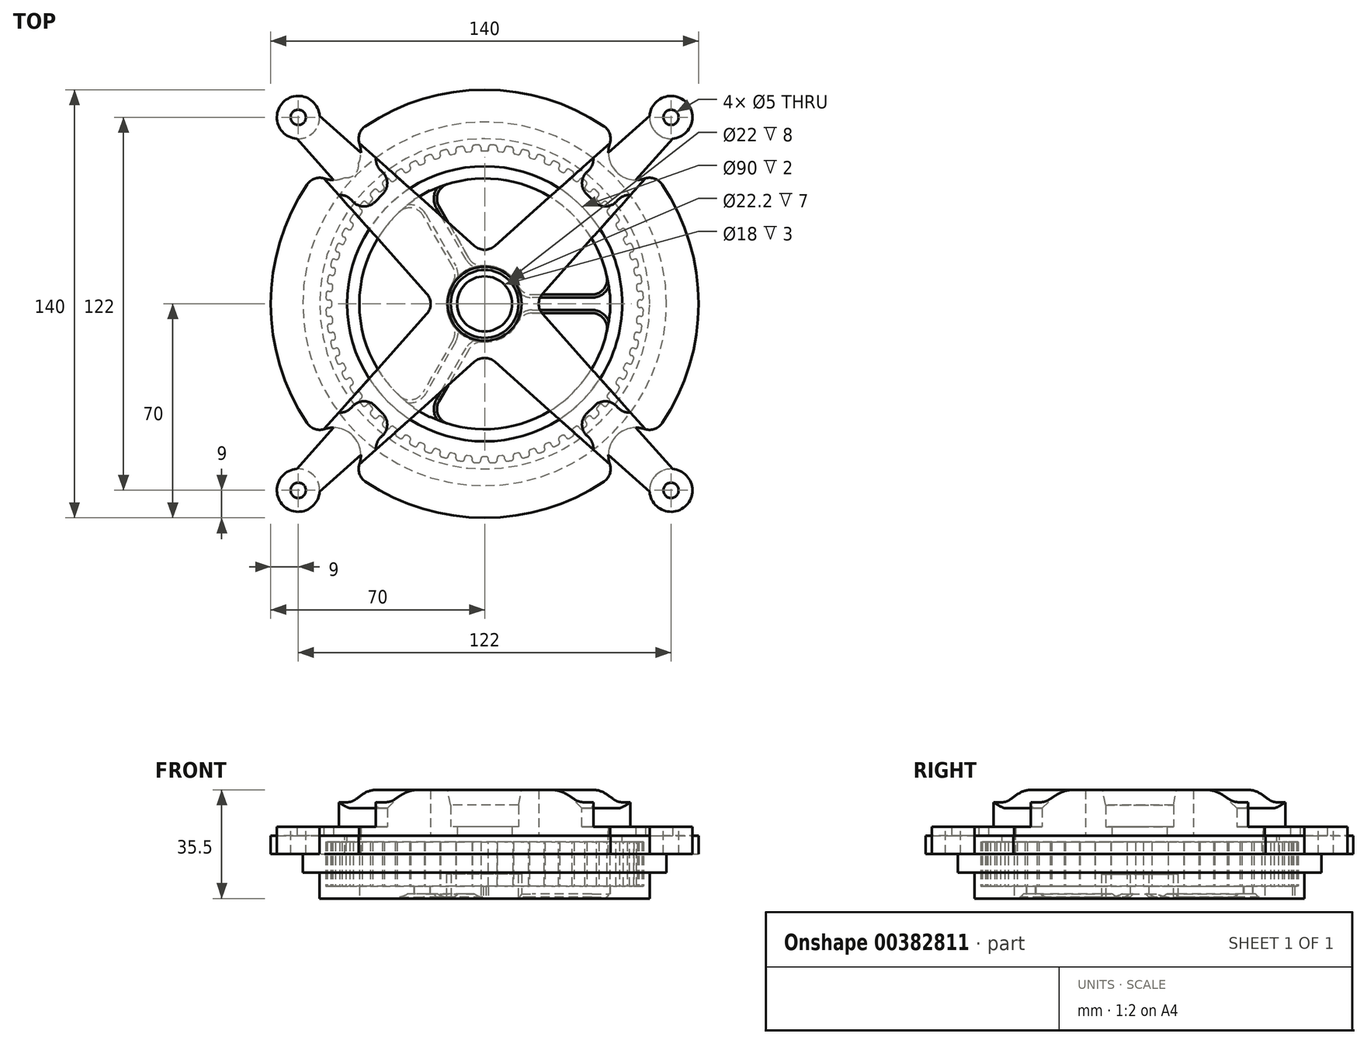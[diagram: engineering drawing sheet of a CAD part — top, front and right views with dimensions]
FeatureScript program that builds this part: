
annotation { "Feature Type Name" : "Feature", "Feature Type Description" : "" }
export const myFeature = defineFeature(function(context is Context, id is Id, definition is map)
    precondition{}
    {
        {
            var Q0;
            Q0=qCreatedBy(makeId("Top.planeOp"),FACE);
            var sketch = newSketch(context, id + "F0", { "sketchPlane" : qUnion([Q0])});
            skCircle(sketch, "E0", {"center": v(0, 0) * mm, "radius": 54 * mm});
            skCircle(sketch, "E1", {"center": v(0, 0) * mm, "radius": 52 * mm});
            skLineSegment(sketch, "E2.bottom", {"start": v(-1.25, 54) * mm, "end": v(1.25, 54) * mm});
            skLineSegment(sketch, "E2.top", {"start": v(-1.25, 50) * mm, "end": v(1.25, 50) * mm});
            skLineSegment(sketch, "E2.left", {"start": v(-1.25, 54) * mm, "end": v(-1.25, 50) * mm});
            skLineSegment(sketch, "E2.right", {"start": v(1.25, 54) * mm, "end": v(1.25, 50) * mm});
            skPoint(sketch, "E2.middle", {"position": v(0, 52) * mm});
            skCircle(sketch, "E3", {"center": v(0, 0) * mm, "radius": 57 * mm});
            skCircle(sketch, "E4", {"center": v(0, 0) * mm, "radius": 41 * mm});
            skCircle(sketch, "E5", {"center": v(0, 0) * mm, "radius": 9 * mm});
            skCircle(sketch, "E6", {"center": v(0, 0) * mm, "radius": 11 * mm});
            skCircle(sketch, "E7", {"center": v(0, 0) * mm, "radius": 12.5 * mm});
            skPoint(sketch, "E8.middle", {"position": v(-23.12, 0) * mm});
            skLineSegment(sketch, "E9.bottom", {"start": v(12.13, 3) * mm, "end": v(41.13, 3) * mm});
            skLineSegment(sketch, "E9.top", {"start": v(12.13, -3) * mm, "end": v(41.13, -3) * mm});
            skLineSegment(sketch, "E9.left", {"start": v(12.13, 3) * mm, "end": v(12.13, -3) * mm});
            skLineSegment(sketch, "E9.right", {"start": v(41.13, 3) * mm, "end": v(41.13, -3) * mm});
            skPoint(sketch, "E9.middle", {"position": v(26.63, 0) * mm});
            skLineSegment(sketch, "E10.1.0", {"start": v(-8.67, 9) * mm, "end": v(-23.17, 34.12) * mm});
            skLineSegment(sketch, "E10.1.1", {"start": v(-3.47, 12) * mm, "end": v(-17.97, 37.12) * mm});
            skLineSegment(sketch, "E10.1.2", {"start": v(-23.17, 34.12) * mm, "end": v(-17.97, 37.12) * mm});
            skLineSegment(sketch, "E10.2.0", {"start": v(-3.47, -12) * mm, "end": v(-17.97, -37.12) * mm});
            skLineSegment(sketch, "E10.2.1", {"start": v(-8.67, -9) * mm, "end": v(-23.17, -34.12) * mm});
            skLineSegment(sketch, "E10.2.2", {"start": v(-17.97, -37.12) * mm, "end": v(-23.17, -34.12) * mm});
            skSolve(sketch);
        }
        {
            var Q0;
            Q0=makeQuery(id+"F0.imprint","IMPRINT",FACE,{"disambiguationData":[TD([[makeQuery(id+"F0.imprint","IMPRINT",EDGE,{"derivedFrom":sQuery(id+"F0.wireOp",EDGE,"E0")}),1.0]])]});
            var Q1;
            {var subQ5=sQuery(id+"F0.wireOp",EDGE,"E2.top");Q1=makeQuery(id+"F0.imprint","IMPRINT",FACE,{"disambiguationData":[TD([[makeQuery(id+"F0.imprint","IMPRINT",EDGE,{"derivedFrom":subQ5}),1.0]])]});}
            var Q2;
            {var subQ0=sQuery(id+"F0.wireOp",EDGE,"E2.right");var subQ1=sQuery(id+"F0.wireOp",EDGE,"E0");var subQ2=makeQuery(id+"F0.imprint","INTERSECT",VERTEX,{"derivedFrom":[subQ1,subQ0]});Q2=makeQuery(id+"F0.imprint","IMPRINT",FACE,{"disambiguationData":[TD([[makeQuery(id+"F0.imprint","IMPRINT",EDGE,{"disambiguationData":[TD([[subQ2,1.0]])],"derivedFrom":subQ1}),1.0]])]});}
            extrude(context, id + "F1", {"entities" : qUnion([Q0, Q1, Q2]), "depth" : 8 * mm});
        }
        {
            var Q0;
            Q0=makeQuery(id+"F1.opExtrude","SWEPT_EDGE",EDGE,{"disambiguationData":[OSD([sQuery(id+"F0.wireOp",EDGE,"E2.top"),sQuery(id+"F0.wireOp",EDGE,"E2.left")])]});
            var Q1;
            Q1=makeQuery(id+"F1.opExtrude","SWEPT_EDGE",EDGE,{"disambiguationData":[OSD([sQuery(id+"F0.wireOp",EDGE,"E2.top"),sQuery(id+"F0.wireOp",EDGE,"E2.right")])]});
            var Q2;
            Q2=makeQuery(id+"F1.opExtrude","SWEPT_EDGE",EDGE,{"disambiguationData":[OSD([sQuery(id+"F0.wireOp",EDGE,"E1"),sQuery(id+"F0.wireOp",EDGE,"E2.left")])]});
            var Q3;
            Q3=makeQuery(id+"F1.opExtrude","SWEPT_EDGE",EDGE,{"disambiguationData":[OSD([sQuery(id+"F0.wireOp",EDGE,"E1"),sQuery(id+"F0.wireOp",EDGE,"E2.right")])]});
            fillet(context, id + "F2", {"entities" : qUnion([Q0, Q1, Q2, Q3]), "radius" : 0.8 * mm, "tangentPropagation" : true, "allowEdgeOverflow" : false});
        }
        {
            var Q0;
            Q0=makeQuery(id+"F1.opExtrude","SWEPT_BODY",BODY,{"disambiguationData":[OSD([sQuery(id+"F0.wireOp",EDGE,"E0"),sQuery(id+"F0.wireOp",EDGE,"E1"),sQuery(id+"F0.wireOp",EDGE,"E2.top"),sQuery(id+"F0.wireOp",EDGE,"E2.left"),sQuery(id+"F0.wireOp",EDGE,"E2.right")])]});
            var Q1;
            Q1=makeQuery(id+"F1.opExtrude","SWEPT_FACE",FACE,{"disambiguationData":[OSD([sQuery(id+"F0.wireOp",EDGE,"E0")])]});
            circularPattern(context, id + "F3", {"operationType" : NewBodyOperationType.ADD, "entities" : qUnion([Q0]), "axis" : qUnion([Q1]), "angle" : 360 * degree, "instanceCount" : 60, "equalSpace" : true});
        }
        {
            var Q0;
            {var subQ0=sQuery(id+"F0.wireOp",EDGE,"E10.1.1");var subQ1=sQuery(id+"F0.wireOp",EDGE,"E4");var subQ2=makeQuery(id+"F0.imprint","INTERSECT",VERTEX,{"derivedFrom":[subQ1,subQ0]});Q0=makeQuery(id+"F0.imprint","IMPRINT",FACE,{"disambiguationData":[TD([[makeQuery(id+"F0.imprint","IMPRINT",EDGE,{"disambiguationData":[TD([[subQ2,-1.0]])],"derivedFrom":subQ1}),1.0]])]});}
            var Q1;
            {var subQ0=sQuery(id+"F0.wireOp",EDGE,"E10.2.1");var subQ1=sQuery(id+"F0.wireOp",EDGE,"E4");var subQ2=makeQuery(id+"F0.imprint","INTERSECT",VERTEX,{"derivedFrom":[subQ1,subQ0]});Q1=makeQuery(id+"F0.imprint","IMPRINT",FACE,{"disambiguationData":[TD([[makeQuery(id+"F0.imprint","IMPRINT",EDGE,{"disambiguationData":[TD([[subQ2,-1.0]])],"derivedFrom":subQ1}),1.0]])]});}
            var Q2;
            {var subQ0=sQuery(id+"F0.wireOp",EDGE,"E9.bottom");var subQ1=sQuery(id+"F0.wireOp",EDGE,"E4");var subQ2=makeQuery(id+"F0.imprint","INTERSECT",VERTEX,{"derivedFrom":[subQ1,subQ0]});Q2=makeQuery(id+"F0.imprint","IMPRINT",FACE,{"disambiguationData":[TD([[makeQuery(id+"F0.imprint","IMPRINT",EDGE,{"disambiguationData":[TD([[subQ2,1.0]])],"derivedFrom":subQ1}),1.0]])]});}
            var Q3;
            {var subQ0=sQuery(id+"F0.wireOp",EDGE,"E10.1.1");var subQ1=sQuery(id+"F0.wireOp",EDGE,"E4");var subQ2=makeQuery(id+"F0.imprint","INTERSECT",VERTEX,{"derivedFrom":[subQ1,subQ0]});Q3=makeQuery(id+"F0.imprint","IMPRINT",FACE,{"disambiguationData":[TD([[makeQuery(id+"F0.imprint","IMPRINT",EDGE,{"disambiguationData":[TD([[subQ2,-1.0]])],"derivedFrom":subQ1}),1.0]])]});}
            var Q4;
            {var subQ0=sQuery(id+"F0.wireOp",EDGE,"E10.2.1");var subQ1=sQuery(id+"F0.wireOp",EDGE,"E4");var subQ2=makeQuery(id+"F0.imprint","INTERSECT",VERTEX,{"derivedFrom":[subQ1,subQ0]});Q4=makeQuery(id+"F0.imprint","IMPRINT",FACE,{"disambiguationData":[TD([[makeQuery(id+"F0.imprint","IMPRINT",EDGE,{"disambiguationData":[TD([[subQ2,-1.0]])],"derivedFrom":subQ1}),1.0]])]});}
            var Q5;
            {var subQ0=sQuery(id+"F0.wireOp",EDGE,"E9.bottom");var subQ1=sQuery(id+"F0.wireOp",EDGE,"E4");var subQ2=makeQuery(id+"F0.imprint","INTERSECT",VERTEX,{"derivedFrom":[subQ1,subQ0]});Q5=makeQuery(id+"F0.imprint","IMPRINT",FACE,{"disambiguationData":[TD([[makeQuery(id+"F0.imprint","IMPRINT",EDGE,{"disambiguationData":[TD([[subQ2,1.0]])],"derivedFrom":subQ1}),1.0]])]});}
            var Q6;
            {var subQ2=sQuery(id+"F0.wireOp",EDGE,"E2.top");Q6=makeQuery(id+"F0.imprint","IMPRINT",FACE,{"disambiguationData":[TD([[makeQuery(id+"F0.imprint","IMPRINT",EDGE,{"derivedFrom":subQ2}),-1.0]])]});}
            var Q7;
            {var subQ2=sQuery(id+"F0.wireOp",EDGE,"E2.top");Q7=makeQuery(id+"F0.imprint","IMPRINT",FACE,{"disambiguationData":[TD([[makeQuery(id+"F0.imprint","IMPRINT",EDGE,{"derivedFrom":subQ2}),-1.0]])]});}
            var Q8;
            {var subQ5=sQuery(id+"F0.wireOp",EDGE,"E10.1.2");Q8=makeQuery(id+"F0.imprint","IMPRINT",FACE,{"disambiguationData":[TD([[makeQuery(id+"F0.imprint","IMPRINT",EDGE,{"derivedFrom":subQ5}),-1.0]])]});}
            var Q9;
            {var subQ0=sQuery(id+"F0.wireOp",EDGE,"E10.1.1");var subQ1=sQuery(id+"F0.wireOp",EDGE,"E4");var subQ2=makeQuery(id+"F0.imprint","INTERSECT",VERTEX,{"derivedFrom":[subQ1,subQ0]});Q9=makeQuery(id+"F0.imprint","IMPRINT",FACE,{"disambiguationData":[TD([[makeQuery(id+"F0.imprint","IMPRINT",EDGE,{"disambiguationData":[TD([[subQ2,-1.0]])],"derivedFrom":subQ1}),1.0]])]});}
            var Q10;
            {var subQ5=sQuery(id+"F0.wireOp",EDGE,"E9.right");Q10=makeQuery(id+"F0.imprint","IMPRINT",FACE,{"disambiguationData":[TD([[makeQuery(id+"F0.imprint","IMPRINT",EDGE,{"derivedFrom":subQ5}),-1.0]])]});}
            var Q11;
            {var subQ5=sQuery(id+"F0.wireOp",EDGE,"E10.2.2");Q11=makeQuery(id+"F0.imprint","IMPRINT",FACE,{"disambiguationData":[TD([[makeQuery(id+"F0.imprint","IMPRINT",EDGE,{"derivedFrom":subQ5}),-1.0]])]});}
            var Q12;
            {var subQ0=sQuery(id+"F0.wireOp",EDGE,"E10.2.1");var subQ1=sQuery(id+"F0.wireOp",EDGE,"E4");var subQ2=makeQuery(id+"F0.imprint","INTERSECT",VERTEX,{"derivedFrom":[subQ1,subQ0]});Q12=makeQuery(id+"F0.imprint","IMPRINT",FACE,{"disambiguationData":[TD([[makeQuery(id+"F0.imprint","IMPRINT",EDGE,{"disambiguationData":[TD([[subQ2,-1.0]])],"derivedFrom":subQ1}),1.0]])]});}
            var Q13;
            Q13=makeQuery(id+"F0.imprint","IMPRINT",FACE,{"disambiguationData":[TD([[makeQuery(id+"F0.imprint","IMPRINT",EDGE,{"derivedFrom":sQuery(id+"F0.wireOp",EDGE,"E6")}),-1.0]])]});
            var Q14;
            {var subQ0=sQuery(id+"F0.wireOp",EDGE,"E9.left");Q14=makeQuery(id+"F0.imprint","IMPRINT",FACE,{"disambiguationData":[TD([[makeQuery(id+"F0.imprint","IMPRINT",EDGE,{"derivedFrom":subQ0}),1.0]])]});}
            var Q15;
            {var subQ0=sQuery(id+"F0.wireOp",EDGE,"E9.bottom");var subQ1=sQuery(id+"F0.wireOp",EDGE,"E4");var subQ2=makeQuery(id+"F0.imprint","INTERSECT",VERTEX,{"derivedFrom":[subQ1,subQ0]});Q15=makeQuery(id+"F0.imprint","IMPRINT",FACE,{"disambiguationData":[TD([[makeQuery(id+"F0.imprint","IMPRINT",EDGE,{"disambiguationData":[TD([[subQ2,1.0]])],"derivedFrom":subQ1}),1.0]])]});}
            extrude(context, id + "F4", {"entities" : qUnion([Q0, Q1, Q2, Q3, Q4, Q5, Q6, Q7, Q8, Q9, Q10, Q11, Q12, Q13, Q14, Q15]), "operationType" : NewBodyOperationType.ADD, "depth" : 1.5 * mm});
        }
        {
            var Q0;
            Q0=makeQuery(id+"F0.imprint","IMPRINT",FACE,{"disambiguationData":[TD([[makeQuery(id+"F0.imprint","IMPRINT",EDGE,{"derivedFrom":sQuery(id+"F0.wireOp",EDGE,"E6")}),-1.0]])]});
            extrude(context, id + "F5", {"entities" : qUnion([Q0]), "operationType" : NewBodyOperationType.ADD, "depth" : 8 * mm});
        }
        {
            var Q0;
            Q0=makeQuery(id+"F4.opExtrude","SWEPT_EDGE",EDGE,{"disambiguationData":[OSD([sQuery(id+"F0.wireOp",EDGE,"E7"),sQuery(id+"F0.wireOp",EDGE,"E10.1.0")])]});
            var Q1;
            Q1=makeQuery(id+"F4.opExtrude","SWEPT_EDGE",EDGE,{"disambiguationData":[OSD([sQuery(id+"F0.wireOp",EDGE,"E7"),sQuery(id+"F0.wireOp",EDGE,"E10.1.1")])]});
            var Q2;
            Q2=makeQuery(id+"F4.opExtrude","SWEPT_EDGE",EDGE,{"disambiguationData":[OSD([sQuery(id+"F0.wireOp",EDGE,"E7"),sQuery(id+"F0.wireOp",EDGE,"E9.bottom"),sQuery(id+"F0.wireOp",EDGE,"E9.left")])]});
            var Q3;
            Q3=makeQuery(id+"F4.opExtrude","SWEPT_EDGE",EDGE,{"disambiguationData":[OSD([sQuery(id+"F0.wireOp",EDGE,"E7"),sQuery(id+"F0.wireOp",EDGE,"E9.top"),sQuery(id+"F0.wireOp",EDGE,"E9.left")])]});
            var Q4;
            Q4=makeQuery(id+"F4.opExtrude","SWEPT_EDGE",EDGE,{"disambiguationData":[OSD([sQuery(id+"F0.wireOp",EDGE,"E7"),sQuery(id+"F0.wireOp",EDGE,"E10.2.0")])]});
            var Q5;
            Q5=makeQuery(id+"F4.opExtrude","SWEPT_EDGE",EDGE,{"disambiguationData":[OSD([sQuery(id+"F0.wireOp",EDGE,"E7"),sQuery(id+"F0.wireOp",EDGE,"E10.2.1")])]});
            var Q6;
            Q6=makeQuery(id+"F4.opExtrude","SWEPT_EDGE",EDGE,{"disambiguationData":[OSD([sQuery(id+"F0.wireOp",EDGE,"E4"),sQuery(id+"F0.wireOp",EDGE,"E10.1.1")])]});
            var Q7;
            Q7=makeQuery(id+"F4.opExtrude","SWEPT_EDGE",EDGE,{"disambiguationData":[OSD([sQuery(id+"F0.wireOp",EDGE,"E4"),sQuery(id+"F0.wireOp",EDGE,"E10.1.0")])]});
            var Q8;
            Q8=makeQuery(id+"F4.opExtrude","SWEPT_EDGE",EDGE,{"disambiguationData":[OSD([sQuery(id+"F0.wireOp",EDGE,"E4"),sQuery(id+"F0.wireOp",EDGE,"E9.top")])]});
            var Q9;
            Q9=makeQuery(id+"F4.opExtrude","SWEPT_EDGE",EDGE,{"disambiguationData":[OSD([sQuery(id+"F0.wireOp",EDGE,"E4"),sQuery(id+"F0.wireOp",EDGE,"E9.bottom")])]});
            var Q10;
            Q10=makeQuery(id+"F4.opExtrude","SWEPT_EDGE",EDGE,{"disambiguationData":[OSD([sQuery(id+"F0.wireOp",EDGE,"E4"),sQuery(id+"F0.wireOp",EDGE,"E10.2.1")])]});
            var Q11;
            Q11=makeQuery(id+"F4.opExtrude","SWEPT_EDGE",EDGE,{"disambiguationData":[OSD([sQuery(id+"F0.wireOp",EDGE,"E4"),sQuery(id+"F0.wireOp",EDGE,"E10.2.0")])]});
            fillet(context, id + "F6", {"entities" : qUnion([Q0, Q1, Q2, Q3, Q4, Q5, Q6, Q7, Q8, Q9, Q10, Q11]), "radius" : 5 * mm, "tangentPropagation" : true, "allowEdgeOverflow" : false});
        }
        {
            var Q0;
            {var subQ0=makeQuery(id+"F1.opExtrude","CAP_FACE",FACE,{"disambiguationData":[OSD([sQuery(id+"F0.wireOp",EDGE,"E0"),sQuery(id+"F0.wireOp",EDGE,"E1"),sQuery(id+"F0.wireOp",EDGE,"E2.top"),sQuery(id+"F0.wireOp",EDGE,"E2.left"),sQuery(id+"F0.wireOp",EDGE,"E2.right")])],"isStart":false});Q0=makeQuery(id+"F3.boolean.opBoolean","MERGE",FACE,{"derivedFrom":[subQ0,makeQuery(id+"F3.opPattern","COPY",FACE,{"derivedFrom":subQ0,"instanceName":"1"}),makeQuery(id+"F3.opPattern","COPY",FACE,{"derivedFrom":subQ0,"instanceName":"2"}),makeQuery(id+"F3.opPattern","COPY",FACE,{"derivedFrom":subQ0,"instanceName":"3"}),makeQuery(id+"F3.opPattern","COPY",FACE,{"derivedFrom":subQ0,"instanceName":"4"}),makeQuery(id+"F3.opPattern","COPY",FACE,{"derivedFrom":subQ0,"instanceName":"5"}),makeQuery(id+"F3.opPattern","COPY",FACE,{"derivedFrom":subQ0,"instanceName":"6"}),makeQuery(id+"F3.opPattern","COPY",FACE,{"derivedFrom":subQ0,"instanceName":"7"}),makeQuery(id+"F3.opPattern","COPY",FACE,{"derivedFrom":subQ0,"instanceName":"8"}),makeQuery(id+"F3.opPattern","COPY",FACE,{"derivedFrom":subQ0,"instanceName":"9"}),makeQuery(id+"F3.opPattern","COPY",FACE,{"derivedFrom":subQ0,"instanceName":"10"}),makeQuery(id+"F3.opPattern","COPY",FACE,{"derivedFrom":subQ0,"instanceName":"11"}),makeQuery(id+"F3.opPattern","COPY",FACE,{"derivedFrom":subQ0,"instanceName":"12"}),makeQuery(id+"F3.opPattern","COPY",FACE,{"derivedFrom":subQ0,"instanceName":"13"}),makeQuery(id+"F3.opPattern","COPY",FACE,{"derivedFrom":subQ0,"instanceName":"14"}),makeQuery(id+"F3.opPattern","COPY",FACE,{"derivedFrom":subQ0,"instanceName":"15"}),makeQuery(id+"F3.opPattern","COPY",FACE,{"derivedFrom":subQ0,"instanceName":"16"}),makeQuery(id+"F3.opPattern","COPY",FACE,{"derivedFrom":subQ0,"instanceName":"17"}),makeQuery(id+"F3.opPattern","COPY",FACE,{"derivedFrom":subQ0,"instanceName":"18"}),makeQuery(id+"F3.opPattern","COPY",FACE,{"derivedFrom":subQ0,"instanceName":"19"}),makeQuery(id+"F3.opPattern","COPY",FACE,{"derivedFrom":subQ0,"instanceName":"20"}),makeQuery(id+"F3.opPattern","COPY",FACE,{"derivedFrom":subQ0,"instanceName":"21"}),makeQuery(id+"F3.opPattern","COPY",FACE,{"derivedFrom":subQ0,"instanceName":"22"}),makeQuery(id+"F3.opPattern","COPY",FACE,{"derivedFrom":subQ0,"instanceName":"23"}),makeQuery(id+"F3.opPattern","COPY",FACE,{"derivedFrom":subQ0,"instanceName":"24"}),makeQuery(id+"F3.opPattern","COPY",FACE,{"derivedFrom":subQ0,"instanceName":"25"}),makeQuery(id+"F3.opPattern","COPY",FACE,{"derivedFrom":subQ0,"instanceName":"26"}),makeQuery(id+"F3.opPattern","COPY",FACE,{"derivedFrom":subQ0,"instanceName":"27"}),makeQuery(id+"F3.opPattern","COPY",FACE,{"derivedFrom":subQ0,"instanceName":"28"}),makeQuery(id+"F3.opPattern","COPY",FACE,{"derivedFrom":subQ0,"instanceName":"29"}),makeQuery(id+"F3.opPattern","COPY",FACE,{"derivedFrom":subQ0,"instanceName":"30"}),makeQuery(id+"F3.opPattern","COPY",FACE,{"derivedFrom":subQ0,"instanceName":"31"}),makeQuery(id+"F3.opPattern","COPY",FACE,{"derivedFrom":subQ0,"instanceName":"32"}),makeQuery(id+"F3.opPattern","COPY",FACE,{"derivedFrom":subQ0,"instanceName":"33"}),makeQuery(id+"F3.opPattern","COPY",FACE,{"derivedFrom":subQ0,"instanceName":"34"}),makeQuery(id+"F3.opPattern","COPY",FACE,{"derivedFrom":subQ0,"instanceName":"35"}),makeQuery(id+"F3.opPattern","COPY",FACE,{"derivedFrom":subQ0,"instanceName":"36"}),makeQuery(id+"F3.opPattern","COPY",FACE,{"derivedFrom":subQ0,"instanceName":"37"}),makeQuery(id+"F3.opPattern","COPY",FACE,{"derivedFrom":subQ0,"instanceName":"38"}),makeQuery(id+"F3.opPattern","COPY",FACE,{"derivedFrom":subQ0,"instanceName":"39"}),makeQuery(id+"F3.opPattern","COPY",FACE,{"derivedFrom":subQ0,"instanceName":"40"}),makeQuery(id+"F3.opPattern","COPY",FACE,{"derivedFrom":subQ0,"instanceName":"41"}),makeQuery(id+"F3.opPattern","COPY",FACE,{"derivedFrom":subQ0,"instanceName":"42"}),makeQuery(id+"F3.opPattern","COPY",FACE,{"derivedFrom":subQ0,"instanceName":"43"}),makeQuery(id+"F3.opPattern","COPY",FACE,{"derivedFrom":subQ0,"instanceName":"44"}),makeQuery(id+"F3.opPattern","COPY",FACE,{"derivedFrom":subQ0,"instanceName":"45"}),makeQuery(id+"F3.opPattern","COPY",FACE,{"derivedFrom":subQ0,"instanceName":"46"}),makeQuery(id+"F3.opPattern","COPY",FACE,{"derivedFrom":subQ0,"instanceName":"47"}),makeQuery(id+"F3.opPattern","COPY",FACE,{"derivedFrom":subQ0,"instanceName":"48"}),makeQuery(id+"F3.opPattern","COPY",FACE,{"derivedFrom":subQ0,"instanceName":"49"}),makeQuery(id+"F3.opPattern","COPY",FACE,{"derivedFrom":subQ0,"instanceName":"50"}),makeQuery(id+"F3.opPattern","COPY",FACE,{"derivedFrom":subQ0,"instanceName":"51"}),makeQuery(id+"F3.opPattern","COPY",FACE,{"derivedFrom":subQ0,"instanceName":"52"}),makeQuery(id+"F3.opPattern","COPY",FACE,{"derivedFrom":subQ0,"instanceName":"53"}),makeQuery(id+"F3.opPattern","COPY",FACE,{"derivedFrom":subQ0,"instanceName":"54"}),makeQuery(id+"F3.opPattern","COPY",FACE,{"derivedFrom":subQ0,"instanceName":"55"}),makeQuery(id+"F3.opPattern","COPY",FACE,{"derivedFrom":subQ0,"instanceName":"56"}),makeQuery(id+"F3.opPattern","COPY",FACE,{"derivedFrom":subQ0,"instanceName":"57"}),makeQuery(id+"F3.opPattern","COPY",FACE,{"derivedFrom":subQ0,"instanceName":"58"}),makeQuery(id+"F3.opPattern","COPY",FACE,{"derivedFrom":subQ0,"instanceName":"59"}),makeQuery(id+"F3.opPattern","COPY",FACE,{"derivedFrom":subQ0,"instanceName":"60"}),makeQuery(id+"F3.opPattern","COPY",FACE,{"derivedFrom":subQ0,"instanceName":"61"}),makeQuery(id+"F3.opPattern","COPY",FACE,{"derivedFrom":subQ0,"instanceName":"62"}),makeQuery(id+"F3.opPattern","COPY",FACE,{"derivedFrom":subQ0,"instanceName":"63"}),makeQuery(id+"F3.opPattern","COPY",FACE,{"derivedFrom":subQ0,"instanceName":"64"}),makeQuery(id+"F3.opPattern","COPY",FACE,{"derivedFrom":subQ0,"instanceName":"65"}),makeQuery(id+"F3.opPattern","COPY",FACE,{"derivedFrom":subQ0,"instanceName":"66"}),makeQuery(id+"F3.opPattern","COPY",FACE,{"derivedFrom":subQ0,"instanceName":"67"}),makeQuery(id+"F3.opPattern","COPY",FACE,{"derivedFrom":subQ0,"instanceName":"68"}),makeQuery(id+"F3.opPattern","COPY",FACE,{"derivedFrom":subQ0,"instanceName":"69"}),makeQuery(id+"F3.opPattern","COPY",FACE,{"derivedFrom":subQ0,"instanceName":"70"}),makeQuery(id+"F3.opPattern","COPY",FACE,{"derivedFrom":subQ0,"instanceName":"71"}),makeQuery(id+"F3.opPattern","COPY",FACE,{"derivedFrom":subQ0,"instanceName":"72"}),makeQuery(id+"F3.opPattern","COPY",FACE,{"derivedFrom":subQ0,"instanceName":"73"}),makeQuery(id+"F3.opPattern","COPY",FACE,{"derivedFrom":subQ0,"instanceName":"74"}),makeQuery(id+"F3.opPattern","COPY",FACE,{"derivedFrom":subQ0,"instanceName":"75"}),makeQuery(id+"F3.opPattern","COPY",FACE,{"derivedFrom":subQ0,"instanceName":"76"}),makeQuery(id+"F3.opPattern","COPY",FACE,{"derivedFrom":subQ0,"instanceName":"77"}),makeQuery(id+"F3.opPattern","COPY",FACE,{"derivedFrom":subQ0,"instanceName":"78"}),makeQuery(id+"F3.opPattern","COPY",FACE,{"derivedFrom":subQ0,"instanceName":"79"}),makeQuery(id+"F3.opPattern","COPY",FACE,{"derivedFrom":subQ0,"instanceName":"80"}),makeQuery(id+"F3.opPattern","COPY",FACE,{"derivedFrom":subQ0,"instanceName":"81"}),makeQuery(id+"F3.opPattern","COPY",FACE,{"derivedFrom":subQ0,"instanceName":"82"}),makeQuery(id+"F3.opPattern","COPY",FACE,{"derivedFrom":subQ0,"instanceName":"83"}),makeQuery(id+"F3.opPattern","COPY",FACE,{"derivedFrom":subQ0,"instanceName":"84"}),makeQuery(id+"F3.opPattern","COPY",FACE,{"derivedFrom":subQ0,"instanceName":"85"}),makeQuery(id+"F3.opPattern","COPY",FACE,{"derivedFrom":subQ0,"instanceName":"86"}),makeQuery(id+"F3.opPattern","COPY",FACE,{"derivedFrom":subQ0,"instanceName":"87"}),makeQuery(id+"F3.opPattern","COPY",FACE,{"derivedFrom":subQ0,"instanceName":"88"}),makeQuery(id+"F3.opPattern","COPY",FACE,{"derivedFrom":subQ0,"instanceName":"89"}),makeQuery(id+"F3.opPattern","COPY",FACE,{"derivedFrom":subQ0,"instanceName":"90"})]});}
            var sketch = newSketch(context, id + "F7", { "sketchPlane" : qUnion([Q0])});
            skLineSegment(sketch, "E11", {"start": v(12.13, 49.97) * mm, "end": v(12.13, 52.62) * mm, "construction": true});
            skLineSegment(sketch, "E12", {"start": v(-42.27, 23.46) * mm, "end": v(-47.45, 25.77) * mm, "construction": true});
            skSolve(sketch);
        }
        {
            var Q0;
            {var subQ6=sQuery(id+"F0.wireOp",EDGE,"E0");Q0=makeQuery(id+"F7.imprint","IMPRINT",FACE,{"disambiguationData":[TD([[makeQuery(id+"F7.imprint","IMPRINT",EDGE,{"derivedFrom":makeQuery(id+"F1.opExtrude","CAP_EDGE",EDGE,{"disambiguationData":[OSD([subQ6])],"isStart":false})}),1.0]])]});}
            extrude(context, id + "F8", {"entities" : qUnion([Q0]), "depth" : 12.5 * mm, "offsetDistance" : 25 * mm});
        }
        {
            var Q0;
            {var subQ0=makeQuery(id+"F1.opExtrude","CAP_FACE",FACE,{"disambiguationData":[OSD([sQuery(id+"F0.wireOp",EDGE,"E0"),sQuery(id+"F0.wireOp",EDGE,"E1"),sQuery(id+"F0.wireOp",EDGE,"E2.top"),sQuery(id+"F0.wireOp",EDGE,"E2.left"),sQuery(id+"F0.wireOp",EDGE,"E2.right")])],"isStart":false});Q0=makeQuery(id+"F3.boolean.opBoolean","MERGE",FACE,{"derivedFrom":[subQ0,makeQuery(id+"F3.opPattern","COPY",FACE,{"derivedFrom":subQ0,"instanceName":"1"}),makeQuery(id+"F3.opPattern","COPY",FACE,{"derivedFrom":subQ0,"instanceName":"2"}),makeQuery(id+"F3.opPattern","COPY",FACE,{"derivedFrom":subQ0,"instanceName":"3"}),makeQuery(id+"F3.opPattern","COPY",FACE,{"derivedFrom":subQ0,"instanceName":"4"}),makeQuery(id+"F3.opPattern","COPY",FACE,{"derivedFrom":subQ0,"instanceName":"5"}),makeQuery(id+"F3.opPattern","COPY",FACE,{"derivedFrom":subQ0,"instanceName":"6"}),makeQuery(id+"F3.opPattern","COPY",FACE,{"derivedFrom":subQ0,"instanceName":"7"}),makeQuery(id+"F3.opPattern","COPY",FACE,{"derivedFrom":subQ0,"instanceName":"8"}),makeQuery(id+"F3.opPattern","COPY",FACE,{"derivedFrom":subQ0,"instanceName":"9"}),makeQuery(id+"F3.opPattern","COPY",FACE,{"derivedFrom":subQ0,"instanceName":"10"}),makeQuery(id+"F3.opPattern","COPY",FACE,{"derivedFrom":subQ0,"instanceName":"11"}),makeQuery(id+"F3.opPattern","COPY",FACE,{"derivedFrom":subQ0,"instanceName":"12"}),makeQuery(id+"F3.opPattern","COPY",FACE,{"derivedFrom":subQ0,"instanceName":"13"}),makeQuery(id+"F3.opPattern","COPY",FACE,{"derivedFrom":subQ0,"instanceName":"14"}),makeQuery(id+"F3.opPattern","COPY",FACE,{"derivedFrom":subQ0,"instanceName":"15"}),makeQuery(id+"F3.opPattern","COPY",FACE,{"derivedFrom":subQ0,"instanceName":"16"}),makeQuery(id+"F3.opPattern","COPY",FACE,{"derivedFrom":subQ0,"instanceName":"17"}),makeQuery(id+"F3.opPattern","COPY",FACE,{"derivedFrom":subQ0,"instanceName":"18"}),makeQuery(id+"F3.opPattern","COPY",FACE,{"derivedFrom":subQ0,"instanceName":"19"}),makeQuery(id+"F3.opPattern","COPY",FACE,{"derivedFrom":subQ0,"instanceName":"20"}),makeQuery(id+"F3.opPattern","COPY",FACE,{"derivedFrom":subQ0,"instanceName":"21"}),makeQuery(id+"F3.opPattern","COPY",FACE,{"derivedFrom":subQ0,"instanceName":"22"}),makeQuery(id+"F3.opPattern","COPY",FACE,{"derivedFrom":subQ0,"instanceName":"23"}),makeQuery(id+"F3.opPattern","COPY",FACE,{"derivedFrom":subQ0,"instanceName":"24"}),makeQuery(id+"F3.opPattern","COPY",FACE,{"derivedFrom":subQ0,"instanceName":"25"}),makeQuery(id+"F3.opPattern","COPY",FACE,{"derivedFrom":subQ0,"instanceName":"26"}),makeQuery(id+"F3.opPattern","COPY",FACE,{"derivedFrom":subQ0,"instanceName":"27"}),makeQuery(id+"F3.opPattern","COPY",FACE,{"derivedFrom":subQ0,"instanceName":"28"}),makeQuery(id+"F3.opPattern","COPY",FACE,{"derivedFrom":subQ0,"instanceName":"29"}),makeQuery(id+"F3.opPattern","COPY",FACE,{"derivedFrom":subQ0,"instanceName":"30"}),makeQuery(id+"F3.opPattern","COPY",FACE,{"derivedFrom":subQ0,"instanceName":"31"}),makeQuery(id+"F3.opPattern","COPY",FACE,{"derivedFrom":subQ0,"instanceName":"32"}),makeQuery(id+"F3.opPattern","COPY",FACE,{"derivedFrom":subQ0,"instanceName":"33"}),makeQuery(id+"F3.opPattern","COPY",FACE,{"derivedFrom":subQ0,"instanceName":"34"}),makeQuery(id+"F3.opPattern","COPY",FACE,{"derivedFrom":subQ0,"instanceName":"35"}),makeQuery(id+"F3.opPattern","COPY",FACE,{"derivedFrom":subQ0,"instanceName":"36"}),makeQuery(id+"F3.opPattern","COPY",FACE,{"derivedFrom":subQ0,"instanceName":"37"}),makeQuery(id+"F3.opPattern","COPY",FACE,{"derivedFrom":subQ0,"instanceName":"38"}),makeQuery(id+"F3.opPattern","COPY",FACE,{"derivedFrom":subQ0,"instanceName":"39"}),makeQuery(id+"F3.opPattern","COPY",FACE,{"derivedFrom":subQ0,"instanceName":"40"}),makeQuery(id+"F3.opPattern","COPY",FACE,{"derivedFrom":subQ0,"instanceName":"41"}),makeQuery(id+"F3.opPattern","COPY",FACE,{"derivedFrom":subQ0,"instanceName":"42"}),makeQuery(id+"F3.opPattern","COPY",FACE,{"derivedFrom":subQ0,"instanceName":"43"}),makeQuery(id+"F3.opPattern","COPY",FACE,{"derivedFrom":subQ0,"instanceName":"44"}),makeQuery(id+"F3.opPattern","COPY",FACE,{"derivedFrom":subQ0,"instanceName":"45"}),makeQuery(id+"F3.opPattern","COPY",FACE,{"derivedFrom":subQ0,"instanceName":"46"}),makeQuery(id+"F3.opPattern","COPY",FACE,{"derivedFrom":subQ0,"instanceName":"47"}),makeQuery(id+"F3.opPattern","COPY",FACE,{"derivedFrom":subQ0,"instanceName":"48"}),makeQuery(id+"F3.opPattern","COPY",FACE,{"derivedFrom":subQ0,"instanceName":"49"}),makeQuery(id+"F3.opPattern","COPY",FACE,{"derivedFrom":subQ0,"instanceName":"50"}),makeQuery(id+"F3.opPattern","COPY",FACE,{"derivedFrom":subQ0,"instanceName":"51"}),makeQuery(id+"F3.opPattern","COPY",FACE,{"derivedFrom":subQ0,"instanceName":"52"}),makeQuery(id+"F3.opPattern","COPY",FACE,{"derivedFrom":subQ0,"instanceName":"53"}),makeQuery(id+"F3.opPattern","COPY",FACE,{"derivedFrom":subQ0,"instanceName":"54"}),makeQuery(id+"F3.opPattern","COPY",FACE,{"derivedFrom":subQ0,"instanceName":"55"}),makeQuery(id+"F3.opPattern","COPY",FACE,{"derivedFrom":subQ0,"instanceName":"56"}),makeQuery(id+"F3.opPattern","COPY",FACE,{"derivedFrom":subQ0,"instanceName":"57"}),makeQuery(id+"F3.opPattern","COPY",FACE,{"derivedFrom":subQ0,"instanceName":"58"}),makeQuery(id+"F3.opPattern","COPY",FACE,{"derivedFrom":subQ0,"instanceName":"59"}),makeQuery(id+"F3.opPattern","COPY",FACE,{"derivedFrom":subQ0,"instanceName":"60"}),makeQuery(id+"F3.opPattern","COPY",FACE,{"derivedFrom":subQ0,"instanceName":"61"}),makeQuery(id+"F3.opPattern","COPY",FACE,{"derivedFrom":subQ0,"instanceName":"62"}),makeQuery(id+"F3.opPattern","COPY",FACE,{"derivedFrom":subQ0,"instanceName":"63"}),makeQuery(id+"F3.opPattern","COPY",FACE,{"derivedFrom":subQ0,"instanceName":"64"}),makeQuery(id+"F3.opPattern","COPY",FACE,{"derivedFrom":subQ0,"instanceName":"65"}),makeQuery(id+"F3.opPattern","COPY",FACE,{"derivedFrom":subQ0,"instanceName":"66"}),makeQuery(id+"F3.opPattern","COPY",FACE,{"derivedFrom":subQ0,"instanceName":"67"}),makeQuery(id+"F3.opPattern","COPY",FACE,{"derivedFrom":subQ0,"instanceName":"68"}),makeQuery(id+"F3.opPattern","COPY",FACE,{"derivedFrom":subQ0,"instanceName":"69"}),makeQuery(id+"F3.opPattern","COPY",FACE,{"derivedFrom":subQ0,"instanceName":"70"}),makeQuery(id+"F3.opPattern","COPY",FACE,{"derivedFrom":subQ0,"instanceName":"71"}),makeQuery(id+"F3.opPattern","COPY",FACE,{"derivedFrom":subQ0,"instanceName":"72"}),makeQuery(id+"F3.opPattern","COPY",FACE,{"derivedFrom":subQ0,"instanceName":"73"}),makeQuery(id+"F3.opPattern","COPY",FACE,{"derivedFrom":subQ0,"instanceName":"74"}),makeQuery(id+"F3.opPattern","COPY",FACE,{"derivedFrom":subQ0,"instanceName":"75"}),makeQuery(id+"F3.opPattern","COPY",FACE,{"derivedFrom":subQ0,"instanceName":"76"}),makeQuery(id+"F3.opPattern","COPY",FACE,{"derivedFrom":subQ0,"instanceName":"77"}),makeQuery(id+"F3.opPattern","COPY",FACE,{"derivedFrom":subQ0,"instanceName":"78"}),makeQuery(id+"F3.opPattern","COPY",FACE,{"derivedFrom":subQ0,"instanceName":"79"}),makeQuery(id+"F3.opPattern","COPY",FACE,{"derivedFrom":subQ0,"instanceName":"80"}),makeQuery(id+"F3.opPattern","COPY",FACE,{"derivedFrom":subQ0,"instanceName":"81"}),makeQuery(id+"F3.opPattern","COPY",FACE,{"derivedFrom":subQ0,"instanceName":"82"}),makeQuery(id+"F3.opPattern","COPY",FACE,{"derivedFrom":subQ0,"instanceName":"83"}),makeQuery(id+"F3.opPattern","COPY",FACE,{"derivedFrom":subQ0,"instanceName":"84"}),makeQuery(id+"F3.opPattern","COPY",FACE,{"derivedFrom":subQ0,"instanceName":"85"}),makeQuery(id+"F3.opPattern","COPY",FACE,{"derivedFrom":subQ0,"instanceName":"86"}),makeQuery(id+"F3.opPattern","COPY",FACE,{"derivedFrom":subQ0,"instanceName":"87"}),makeQuery(id+"F3.opPattern","COPY",FACE,{"derivedFrom":subQ0,"instanceName":"88"}),makeQuery(id+"F3.opPattern","COPY",FACE,{"derivedFrom":subQ0,"instanceName":"89"}),makeQuery(id+"F3.opPattern","COPY",FACE,{"derivedFrom":subQ0,"instanceName":"90"}),makeQuery(id+"F3.opPattern","COPY",FACE,{"derivedFrom":subQ0,"instanceName":"91"})]});}
            extrude(context, id + "F9", {"entities" : qUnion([Q0]), "operationType" : NewBodyOperationType.ADD, "depth" : 4 * mm});
        }
        {
            var Q0;
            Q0=makeQuery(id+"F4.opExtrude","CAP_EDGE",EDGE,{"disambiguationData":[OSD([sQuery(id+"F0.wireOp",EDGE,"E9.top")])],"isStart":false});
            var Q1;
            Q1=makeQuery(id+"F4.opExtrude","CAP_EDGE",EDGE,{"disambiguationData":[OSD([sQuery(id+"F0.wireOp",EDGE,"E10.2.1")])],"isStart":false});
            var Q2;
            Q2=makeQuery(id+"F4.opExtrude","CAP_EDGE",EDGE,{"disambiguationData":[OSD([sQuery(id+"F0.wireOp",EDGE,"E9.bottom")])],"isStart":false});
            chamfer(context, id + "F10", {"entities" : qUnion([Q0, Q1, Q2]), "width" : 1 * mm, "tangentPropagation" : true});
        }
        {
            var Q0;
            {var subQ2=sQuery(id+"F0.wireOp",EDGE,"E2.top");Q0=makeQuery(id+"F0.imprint","IMPRINT",FACE,{"disambiguationData":[TD([[makeQuery(id+"F0.imprint","IMPRINT",EDGE,{"derivedFrom":subQ2}),-1.0]])]});}
            extrude(context, id + "F11", {"entities" : qUnion([Q0]), "operationType" : NewBodyOperationType.ADD, "depth" : 4 * mm});
        }
        {
            var Q0;
            Q0=makeQuery(id+"F8.opExtrude","CAP_FACE",FACE,{"disambiguationData":[OSD([sQuery(id+"F0.wireOp",EDGE,"E0"),sQuery(id+"F0.wireOp",EDGE,"E1"),sQuery(id+"F0.wireOp",EDGE,"E2.top"),sQuery(id+"F0.wireOp",EDGE,"E2.left"),sQuery(id+"F0.wireOp",EDGE,"E2.right")])],"isStart":false});
            var sketch = newSketch(context, id + "F12", { "sketchPlane" : qUnion([Q0])});
            skCircle(sketch, "E13", {"center": v(0, 0) * mm, "radius": 59.5 * mm});
            skCircle(sketch, "E14.0", {"center": v(0, 0) * mm, "radius": 54 * mm});
            skCircle(sketch, "E15", {"center": v(0, 0) * mm, "radius": 45 * mm});
            skCircle(sketch, "E16", {"center": v(0, 0) * mm, "radius": 58 * mm});
            skPoint(sketch, "E17.middle", {"position": v(0, 54) * mm});
            skCircle(sketch, "E18", {"center": v(0, 0) * mm, "radius": 70 * mm});
            skLineSegment(sketch, "E19.bottom", {"start": v(-61, 61) * mm, "end": v(61, 61) * mm, "construction": true});
            skLineSegment(sketch, "E19.top", {"start": v(-61, -61) * mm, "end": v(61, -61) * mm, "construction": true});
            skLineSegment(sketch, "E19.left", {"start": v(-61, 61) * mm, "end": v(-61, -61) * mm, "construction": true});
            skLineSegment(sketch, "E19.right", {"start": v(61, 61) * mm, "end": v(61, -61) * mm, "construction": true});
            skCircle(sketch, "E20", {"center": v(-61, 61) * mm, "radius": 2.5 * mm});
            skCircle(sketch, "E21", {"center": v(61, 61) * mm, "radius": 2.5 * mm});
            skCircle(sketch, "E22", {"center": v(61, -61) * mm, "radius": 2.5 * mm});
            skCircle(sketch, "E23", {"center": v(-61, -61) * mm, "radius": 2.5 * mm});
            skCircle(sketch, "E24", {"center": v(-61, 61) * mm, "radius": 7 * mm});
            skCircle(sketch, "E25", {"center": v(61, 61) * mm, "radius": 7 * mm});
            skCircle(sketch, "E26", {"center": v(61, -61) * mm, "radius": 7 * mm});
            skCircle(sketch, "E27", {"center": v(-61, -61) * mm, "radius": 7 * mm});
            skLineSegment(sketch, "E28", {"start": v(-61.7, 33.08) * mm, "end": v(-67.82, 59.41) * mm});
            skLineSegment(sketch, "E29", {"start": v(-33.08, 61.7) * mm, "end": v(-59.41, 67.82) * mm});
            skLineSegment(sketch, "E30", {"start": v(33.08, 61.7) * mm, "end": v(59.41, 67.82) * mm});
            skLineSegment(sketch, "E31", {"start": v(-61.7, -33.08) * mm, "end": v(-67.82, -59.41) * mm});
            skLineSegment(sketch, "E32", {"start": v(-33.08, -61.7) * mm, "end": v(-59.41, -67.82) * mm});
            skLineSegment(sketch, "E33", {"start": v(61.7, 33.08) * mm, "end": v(67.82, 59.41) * mm});
            skLineSegment(sketch, "E34", {"start": v(61.7, -33.08) * mm, "end": v(67.82, -59.41) * mm});
            skLineSegment(sketch, "E35", {"start": v(33.08, -61.7) * mm, "end": v(59.41, -67.82) * mm});
            skPoint(sketch, "E36.orphan", {"position": v(-54, 0) * mm});
            skPoint(sketch, "E37.orphan", {"position": v(54, 0) * mm});
            skPoint(sketch, "E38.orphan", {"position": v(0, -54) * mm});
            skLineSegment(sketch, "E39", {"start": v(61, 61) * mm, "end": v(-61, -61) * mm, "construction": true});
            skLineSegment(sketch, "E40", {"start": v(-61, 61) * mm, "end": v(61, -61) * mm, "construction": true});
            skLineSegment(sketch, "E41", {"start": v(-49.5, 49.5) * mm, "end": v(-41.01, 41.01) * mm, "construction": true});
            skCircle(sketch, "E42", {"center": v(49.5, 49.5) * mm, "radius": 9 * mm});
            skCircle(sketch, "E43", {"center": v(-45.25, 45.25) * mm, "radius": 4 * mm});
            skCircle(sketch, "E44.1.0", {"center": v(-49.5, 49.5) * mm, "radius": 9 * mm});
            skCircle(sketch, "E44.2.0", {"center": v(-49.5, -49.5) * mm, "radius": 9 * mm});
            skCircle(sketch, "E44.3.0", {"center": v(49.5, -49.5) * mm, "radius": 9 * mm});
            skSolve(sketch);
        }
        {
            var Q0;
            {var subQ0=sQuery(id+"F12.wireOp",EDGE,"mK7cAFdZ-tF4r-BnAY-2Sz0-cZjIgqzOGccH");var subQ1=sQuery(id+"F12.wireOp",EDGE,"E13");var subQ2=makeQuery(id+"F12.imprint","INTERSECT",VERTEX,{"disambiguationData":[OD(0.0)],"derivedFrom":[subQ1,subQ0]});Q0=makeQuery(id+"F12.imprint","IMPRINT",FACE,{"disambiguationData":[TD([[makeQuery(id+"F12.imprint","IMPRINT",EDGE,{"disambiguationData":[TD([[subQ2,-1.0]])],"derivedFrom":subQ1}),1.0]])]});}
            var Q1;
            {var subQ0=sQuery(id+"F12.wireOp",EDGE,"6ZHCmnEN-hGg1-kFDm-vIRD-UXKnUUiogvO6");var subQ1=sQuery(id+"F12.wireOp",EDGE,"E13");var subQ2=makeQuery(id+"F12.imprint","INTERSECT",VERTEX,{"disambiguationData":[OD(0.0)],"derivedFrom":[subQ1,subQ0]});Q1=makeQuery(id+"F12.imprint","IMPRINT",FACE,{"disambiguationData":[TD([[makeQuery(id+"F12.imprint","IMPRINT",EDGE,{"disambiguationData":[TD([[subQ2,-1.0]])],"derivedFrom":subQ1}),1.0]])]});}
            var Q2;
            {var subQ0=sQuery(id+"F12.wireOp",EDGE,"jWrBxqxo-wktR-lxVl-3Y0r-I2q5EdXb6ge5");var subQ1=sQuery(id+"F12.wireOp",EDGE,"E13");var subQ2=makeQuery(id+"F12.imprint","INTERSECT",VERTEX,{"disambiguationData":[OD(0.0)],"derivedFrom":[subQ1,subQ0]});Q2=makeQuery(id+"F12.imprint","IMPRINT",FACE,{"disambiguationData":[TD([[makeQuery(id+"F12.imprint","IMPRINT",EDGE,{"disambiguationData":[TD([[subQ2,1.0]])],"derivedFrom":subQ1}),1.0]])]});}
            var Q3;
            Q3=makeQuery(id+"F12.imprint","IMPRINT",FACE,{"disambiguationData":[TD([[makeQuery(id+"F12.imprint","IMPRINT",EDGE,{"derivedFrom":sQuery(id+"F12.wireOp",EDGE,"E15")}),-1.0]])]});
            var Q4;
            {var subQ0=sQuery(id+"F12.wireOp",EDGE,"mK7cAFdZ-tF4r-BnAY-2Sz0-cZjIgqzOGccH");var subQ1=sQuery(id+"F12.wireOp",EDGE,"E13");var subQ2=makeQuery(id+"F12.imprint","INTERSECT",VERTEX,{"disambiguationData":[OD(1.0)],"derivedFrom":[subQ1,subQ0]});Q4=makeQuery(id+"F12.imprint","IMPRINT",FACE,{"disambiguationData":[TD([[makeQuery(id+"F12.imprint","IMPRINT",EDGE,{"disambiguationData":[TD([[subQ2,-1.0]])],"derivedFrom":subQ1}),1.0]])]});}
            var Q5;
            {var subQ0=sQuery(id+"F12.wireOp",EDGE,"A9ctRC3Q-p3it-8eQD-YH8h-ly8p0Lvc9ygV");var subQ1=sQuery(id+"F12.wireOp",EDGE,"E13");var subQ2=makeQuery(id+"F12.imprint","INTERSECT",VERTEX,{"disambiguationData":[OD(0.0)],"derivedFrom":[subQ1,subQ0]});Q5=makeQuery(id+"F12.imprint","IMPRINT",FACE,{"disambiguationData":[TD([[makeQuery(id+"F12.imprint","IMPRINT",EDGE,{"disambiguationData":[TD([[subQ2,-1.0]])],"derivedFrom":subQ1}),-1.0]])]});}
            var Q6;
            {var subQ0=sQuery(id+"F12.wireOp",EDGE,"A9ctRC3Q-p3it-8eQD-YH8h-ly8p0Lvc9ygV");var subQ1=sQuery(id+"F12.wireOp",EDGE,"E13");var subQ2=makeQuery(id+"F12.imprint","INTERSECT",VERTEX,{"disambiguationData":[OD(1.0)],"derivedFrom":[subQ1,subQ0]});Q6=makeQuery(id+"F12.imprint","IMPRINT",FACE,{"disambiguationData":[TD([[makeQuery(id+"F12.imprint","IMPRINT",EDGE,{"disambiguationData":[TD([[subQ2,-1.0]])],"derivedFrom":subQ1}),1.0]])]});}
            var Q7;
            {var subQ0=sQuery(id+"F12.wireOp",EDGE,"6ZHCmnEN-hGg1-kFDm-vIRD-UXKnUUiogvO6");var subQ1=sQuery(id+"F12.wireOp",EDGE,"E13");var subQ2=makeQuery(id+"F12.imprint","INTERSECT",VERTEX,{"disambiguationData":[OD(0.0)],"derivedFrom":[subQ1,subQ0]});Q7=makeQuery(id+"F12.imprint","IMPRINT",FACE,{"disambiguationData":[TD([[makeQuery(id+"F12.imprint","IMPRINT",EDGE,{"disambiguationData":[TD([[subQ2,-1.0]])],"derivedFrom":subQ1}),-1.0]])]});}
            var Q8;
            {var subQ0=sQuery(id+"F12.wireOp",EDGE,"6ZHCmnEN-hGg1-kFDm-vIRD-UXKnUUiogvO6");var subQ1=sQuery(id+"F12.wireOp",EDGE,"E13");var subQ2=makeQuery(id+"F12.imprint","INTERSECT",VERTEX,{"disambiguationData":[OD(1.0)],"derivedFrom":[subQ1,subQ0]});Q8=makeQuery(id+"F12.imprint","IMPRINT",FACE,{"disambiguationData":[TD([[makeQuery(id+"F12.imprint","IMPRINT",EDGE,{"disambiguationData":[TD([[subQ2,-1.0]])],"derivedFrom":subQ1}),1.0]])]});}
            var Q9;
            {var subQ0=sQuery(id+"F12.wireOp",EDGE,"jWrBxqxo-wktR-lxVl-3Y0r-I2q5EdXb6ge5");var subQ1=sQuery(id+"F12.wireOp",EDGE,"E13");var subQ2=makeQuery(id+"F12.imprint","INTERSECT",VERTEX,{"disambiguationData":[OD(0.0)],"derivedFrom":[subQ1,subQ0]});Q9=makeQuery(id+"F12.imprint","IMPRINT",FACE,{"disambiguationData":[TD([[makeQuery(id+"F12.imprint","IMPRINT",EDGE,{"disambiguationData":[TD([[subQ2,1.0]])],"derivedFrom":subQ1}),-1.0]])]});}
            var Q10;
            {var subQ0=sQuery(id+"F12.wireOp",EDGE,"mK7cAFdZ-tF4r-BnAY-2Sz0-cZjIgqzOGccH");var subQ1=sQuery(id+"F12.wireOp",EDGE,"E13");var subQ2=makeQuery(id+"F12.imprint","INTERSECT",VERTEX,{"disambiguationData":[OD(0.0)],"derivedFrom":[subQ1,subQ0]});Q10=makeQuery(id+"F12.imprint","IMPRINT",FACE,{"disambiguationData":[TD([[makeQuery(id+"F12.imprint","IMPRINT",EDGE,{"disambiguationData":[TD([[subQ2,1.0]])],"derivedFrom":subQ1}),1.0]])]});}
            var Q11;
            {var subQ0=sQuery(id+"F12.wireOp",EDGE,"A9ctRC3Q-p3it-8eQD-YH8h-ly8p0Lvc9ygV");var subQ1=sQuery(id+"F12.wireOp",EDGE,"E13");var subQ2=makeQuery(id+"F12.imprint","INTERSECT",VERTEX,{"disambiguationData":[OD(0.0)],"derivedFrom":[subQ1,subQ0]});Q11=makeQuery(id+"F12.imprint","IMPRINT",FACE,{"disambiguationData":[TD([[makeQuery(id+"F12.imprint","IMPRINT",EDGE,{"disambiguationData":[TD([[subQ2,-1.0]])],"derivedFrom":subQ1}),1.0]])]});}
            var Q12;
            {var subQ0=sQuery(id+"F12.wireOp",EDGE,"mK7cAFdZ-tF4r-BnAY-2Sz0-cZjIgqzOGccH");var subQ1=sQuery(id+"F12.wireOp",EDGE,"E13");var subQ2=makeQuery(id+"F12.imprint","INTERSECT",VERTEX,{"disambiguationData":[OD(0.0)],"derivedFrom":[subQ1,subQ0]});Q12=makeQuery(id+"F12.imprint","IMPRINT",FACE,{"disambiguationData":[TD([[makeQuery(id+"F12.imprint","IMPRINT",EDGE,{"disambiguationData":[TD([[subQ2,-1.0]])],"derivedFrom":subQ1}),-1.0]])]});}
            var Q13;
            {var subQ0=sQuery(id+"F12.wireOp",EDGE,"mK7cAFdZ-tF4r-BnAY-2Sz0-cZjIgqzOGccH");var subQ1=sQuery(id+"F12.wireOp",EDGE,"E14.0");var subQ2=makeQuery(id+"F12.imprint","INTERSECT",VERTEX,{"derivedFrom":[subQ1,subQ0]});Q13=makeQuery(id+"F12.imprint","IMPRINT",FACE,{"disambiguationData":[TD([[makeQuery(id+"F12.imprint","IMPRINT",EDGE,{"disambiguationData":[TD([[subQ2,-1.0]])],"derivedFrom":subQ1}),-1.0]])]});}
            var Q14;
            {var subQ0=sQuery(id+"F12.wireOp",EDGE,"mK7cAFdZ-tF4r-BnAY-2Sz0-cZjIgqzOGccH");var subQ1=makeQuery(id+"F12.imprint","INTERSECT",VERTEX,{"derivedFrom":[sQuery(id+"F12.wireOp",EDGE,"E14.0"),subQ0]});Q14=makeQuery(id+"F12.imprint","IMPRINT",FACE,{"disambiguationData":[TD([[makeQuery(id+"F12.imprint","IMPRINT",EDGE,{"disambiguationData":[TD([[subQ1,1.0]])],"derivedFrom":subQ0}),1.0]])]});}
            var Q15;
            {var subQ0=sQuery(id+"F12.wireOp",EDGE,"A9ctRC3Q-p3it-8eQD-YH8h-ly8p0Lvc9ygV");var subQ1=makeQuery(id+"F12.imprint","INTERSECT",VERTEX,{"derivedFrom":[sQuery(id+"F12.wireOp",EDGE,"E14.0"),subQ0]});Q15=makeQuery(id+"F12.imprint","IMPRINT",FACE,{"disambiguationData":[TD([[makeQuery(id+"F12.imprint","IMPRINT",EDGE,{"disambiguationData":[TD([[subQ1,-1.0]])],"derivedFrom":subQ0}),1.0]])]});}
            var Q16;
            {var subQ0=sQuery(id+"F12.wireOp",EDGE,"A9ctRC3Q-p3it-8eQD-YH8h-ly8p0Lvc9ygV");var subQ1=sQuery(id+"F12.wireOp",EDGE,"E14.0");var subQ2=makeQuery(id+"F12.imprint","INTERSECT",VERTEX,{"derivedFrom":[subQ1,subQ0]});Q16=makeQuery(id+"F12.imprint","IMPRINT",FACE,{"disambiguationData":[TD([[makeQuery(id+"F12.imprint","IMPRINT",EDGE,{"disambiguationData":[TD([[subQ2,-1.0]])],"derivedFrom":subQ1}),-1.0]])]});}
            var Q17;
            {var subQ0=sQuery(id+"F12.wireOp",EDGE,"6ZHCmnEN-hGg1-kFDm-vIRD-UXKnUUiogvO6");var subQ1=makeQuery(id+"F12.imprint","INTERSECT",VERTEX,{"derivedFrom":[sQuery(id+"F12.wireOp",EDGE,"E14.0"),subQ0]});Q17=makeQuery(id+"F12.imprint","IMPRINT",FACE,{"disambiguationData":[TD([[makeQuery(id+"F12.imprint","IMPRINT",EDGE,{"disambiguationData":[TD([[subQ1,1.0]])],"derivedFrom":subQ0}),1.0]])]});}
            var Q18;
            {var subQ0=sQuery(id+"F12.wireOp",EDGE,"jWrBxqxo-wktR-lxVl-3Y0r-I2q5EdXb6ge5");var subQ1=sQuery(id+"F12.wireOp",EDGE,"E14.0");var subQ2=makeQuery(id+"F12.imprint","INTERSECT",VERTEX,{"derivedFrom":[subQ1,subQ0]});Q18=makeQuery(id+"F12.imprint","IMPRINT",FACE,{"disambiguationData":[TD([[makeQuery(id+"F12.imprint","IMPRINT",EDGE,{"disambiguationData":[TD([[subQ2,1.0]])],"derivedFrom":subQ1}),-1.0]])]});}
            var Q19;
            {var subQ0=sQuery(id+"F12.wireOp",EDGE,"jWrBxqxo-wktR-lxVl-3Y0r-I2q5EdXb6ge5");var subQ1=makeQuery(id+"F12.imprint","INTERSECT",VERTEX,{"derivedFrom":[sQuery(id+"F12.wireOp",EDGE,"E14.0"),subQ0]});Q19=makeQuery(id+"F12.imprint","IMPRINT",FACE,{"disambiguationData":[TD([[makeQuery(id+"F12.imprint","IMPRINT",EDGE,{"disambiguationData":[TD([[subQ1,1.0]])],"derivedFrom":subQ0}),1.0]])]});}
            var Q20;
            {var subQ0=sQuery(id+"F12.wireOp",EDGE,"mK7cAFdZ-tF4r-BnAY-2Sz0-cZjIgqzOGccH");var subQ1=sQuery(id+"F12.wireOp",EDGE,"E14.0");var subQ2=makeQuery(id+"F12.imprint","INTERSECT",VERTEX,{"derivedFrom":[subQ1,subQ0]});Q20=makeQuery(id+"F12.imprint","IMPRINT",FACE,{"disambiguationData":[TD([[makeQuery(id+"F12.imprint","IMPRINT",EDGE,{"disambiguationData":[TD([[subQ2,1.0]])],"derivedFrom":subQ1}),-1.0]])]});}
            var Q21;
            {var subQ0=sQuery(id+"F12.wireOp",EDGE,"044f241d-f53a-4093-93dc-326870641880.1.1");var subQ1=sQuery(id+"F12.wireOp",EDGE,"E14.0");var subQ2=makeQuery(id+"F12.imprint","INTERSECT",VERTEX,{"derivedFrom":[subQ1,subQ0]});Q21=makeQuery(id+"F12.imprint","IMPRINT",FACE,{"disambiguationData":[TD([[makeQuery(id+"F12.imprint","IMPRINT",EDGE,{"disambiguationData":[TD([[subQ2,-1.0]])],"derivedFrom":subQ1}),-1.0]])]});}
            var Q22;
            {var subQ0=sQuery(id+"F12.wireOp",EDGE,"044f241d-f53a-4093-93dc-326870641880.2.1");var subQ1=sQuery(id+"F12.wireOp",EDGE,"E14.0");var subQ2=makeQuery(id+"F12.imprint","INTERSECT",VERTEX,{"derivedFrom":[subQ1,subQ0]});Q22=makeQuery(id+"F12.imprint","IMPRINT",FACE,{"disambiguationData":[TD([[makeQuery(id+"F12.imprint","IMPRINT",EDGE,{"disambiguationData":[TD([[subQ2,-1.0]])],"derivedFrom":subQ1}),-1.0]])]});}
            var Q23;
            {var subQ0=sQuery(id+"F12.wireOp",EDGE,"6ZHCmnEN-hGg1-kFDm-vIRD-UXKnUUiogvO6");var subQ1=sQuery(id+"F12.wireOp",EDGE,"E14.0");var subQ2=makeQuery(id+"F12.imprint","INTERSECT",VERTEX,{"derivedFrom":[subQ1,subQ0]});Q23=makeQuery(id+"F12.imprint","IMPRINT",FACE,{"disambiguationData":[TD([[makeQuery(id+"F12.imprint","IMPRINT",EDGE,{"disambiguationData":[TD([[subQ2,-1.0]])],"derivedFrom":subQ1}),-1.0]])]});}
            var Q24;
            {var subQ0=sQuery(id+"F12.wireOp",EDGE,"044f241d-f53a-4093-93dc-326870641880.3.0");var subQ1=sQuery(id+"F12.wireOp",EDGE,"E14.0");var subQ2=makeQuery(id+"F12.imprint","INTERSECT",VERTEX,{"derivedFrom":[subQ1,subQ0]});Q24=makeQuery(id+"F12.imprint","IMPRINT",FACE,{"disambiguationData":[TD([[makeQuery(id+"F12.imprint","IMPRINT",EDGE,{"disambiguationData":[TD([[subQ2,1.0]])],"derivedFrom":subQ1}),-1.0]])]});}
            extrude(context, id + "F13", {"entities" : qUnion([Q0, Q1, Q2, Q3, Q4, Q5, Q6, Q7, Q8, Q9, Q10, Q11, Q12, Q13, Q14, Q15, Q16, Q17, Q18, Q19, Q20, Q21, Q22, Q23, Q24]), "operationType" : NewBodyOperationType.ADD, "oppositeDirection" : true, "depth" : 2 * mm});
        }
        {
            var Q0;
            Q0=makeQuery(id+"F12.imprint","IMPRINT",FACE,{"disambiguationData":[TD([[makeQuery(id+"F12.imprint","IMPRINT",EDGE,{"derivedFrom":sQuery(id+"F12.wireOp",EDGE,"E14.0")}),-1.0]])]});
            var Q1;
            Q1=makeQuery(id+"F12.imprint","IMPRINT",FACE,{"disambiguationData":[TD([[makeQuery(id+"F12.imprint","IMPRINT",EDGE,{"derivedFrom":sQuery(id+"F12.wireOp",EDGE,"E13")}),1.0]])]});
            extrude(context, id + "F14", {"entities" : qUnion([Q0, Q1]), "operationType" : NewBodyOperationType.ADD, "oppositeDirection" : true, "depth" : 12 * mm, "offsetDistance" : 25 * mm});
        }
        {
            var Q0;
            {var subQ0=sQuery(id+"F12.wireOp",EDGE,"E31");Q0=makeQuery(id+"F12.imprint","IMPRINT",FACE,{"disambiguationData":[TD([[makeQuery(id+"F12.imprint","IMPRINT",EDGE,{"derivedFrom":subQ0}),1.0]])]});}
            var Q1;
            {var subQ0=sQuery(id+"F12.wireOp",EDGE,"E34");Q1=makeQuery(id+"F12.imprint","IMPRINT",FACE,{"disambiguationData":[TD([[makeQuery(id+"F12.imprint","IMPRINT",EDGE,{"derivedFrom":subQ0}),-1.0]])]});}
            var Q2;
            Q2=makeQuery(id+"F12.imprint","IMPRINT",FACE,{"disambiguationData":[TD([[makeQuery(id+"F12.imprint","IMPRINT",EDGE,{"derivedFrom":sQuery(id+"F12.wireOp",EDGE,"E23")}),-1.0]])]});
            var Q3;
            Q3=makeQuery(id+"F12.imprint","IMPRINT",FACE,{"disambiguationData":[TD([[makeQuery(id+"F12.imprint","IMPRINT",EDGE,{"derivedFrom":sQuery(id+"F12.wireOp",EDGE,"E22")}),-1.0]])]});
            var Q4;
            Q4=makeQuery(id+"F12.imprint","IMPRINT",FACE,{"disambiguationData":[TD([[makeQuery(id+"F12.imprint","IMPRINT",EDGE,{"derivedFrom":sQuery(id+"F12.wireOp",EDGE,"E21")}),-1.0]])]});
            var Q5;
            Q5=makeQuery(id+"F12.imprint","IMPRINT",FACE,{"disambiguationData":[TD([[makeQuery(id+"F12.imprint","IMPRINT",EDGE,{"derivedFrom":sQuery(id+"F12.wireOp",EDGE,"E20")}),-1.0]])]});
            var Q6;
            {var subQ0=sQuery(id+"F12.wireOp",EDGE,"E28");Q6=makeQuery(id+"F12.imprint","IMPRINT",FACE,{"disambiguationData":[TD([[makeQuery(id+"F12.imprint","IMPRINT",EDGE,{"derivedFrom":subQ0}),-1.0]])]});}
            var Q7;
            {var subQ0=sQuery(id+"F12.wireOp",EDGE,"E30");Q7=makeQuery(id+"F12.imprint","IMPRINT",FACE,{"disambiguationData":[TD([[makeQuery(id+"F12.imprint","IMPRINT",EDGE,{"derivedFrom":subQ0}),-1.0]])]});}
            var Q8;
            Q8=makeQuery(id+"F12.imprint","IMPRINT",FACE,{"disambiguationData":[TD([[makeQuery(id+"F12.imprint","IMPRINT",EDGE,{"derivedFrom":sQuery(id+"F12.wireOp",EDGE,"E13")}),-1.0]])]});
            extrude(context, id + "F15", {"entities" : qUnion([Q0, Q1, Q2, Q3, Q4, Q5, Q6, Q7, Q8]), "operationType" : NewBodyOperationType.ADD, "oppositeDirection" : true, "depth" : 6 * mm, "offsetDistance" : 25 * mm});
        }
        {
            var Q0;
            Q0=makeQuery(id+"F15.opExtrude","SWEPT_EDGE",EDGE,{"disambiguationData":[OSD([sQuery(id+"F12.wireOp",EDGE,"E18"),sQuery(id+"F12.wireOp",EDGE,"E31")])]});
            var Q1;
            Q1=makeQuery(id+"F15.opExtrude","SWEPT_EDGE",EDGE,{"disambiguationData":[OSD([sQuery(id+"F12.wireOp",EDGE,"E18"),sQuery(id+"F12.wireOp",EDGE,"E28")])]});
            var Q2;
            Q2=makeQuery(id+"F15.opExtrude","SWEPT_EDGE",EDGE,{"disambiguationData":[OSD([sQuery(id+"F12.wireOp",EDGE,"E18"),sQuery(id+"F12.wireOp",EDGE,"E29")])]});
            var Q3;
            Q3=makeQuery(id+"F15.opExtrude","SWEPT_EDGE",EDGE,{"disambiguationData":[OSD([sQuery(id+"F12.wireOp",EDGE,"E18"),sQuery(id+"F12.wireOp",EDGE,"E30")])]});
            var Q4;
            Q4=makeQuery(id+"F15.opExtrude","SWEPT_EDGE",EDGE,{"disambiguationData":[OSD([sQuery(id+"F12.wireOp",EDGE,"E18"),sQuery(id+"F12.wireOp",EDGE,"E33")])]});
            var Q5;
            Q5=makeQuery(id+"F15.opExtrude","SWEPT_EDGE",EDGE,{"disambiguationData":[OSD([sQuery(id+"F12.wireOp",EDGE,"E18"),sQuery(id+"F12.wireOp",EDGE,"E34")])]});
            var Q6;
            Q6=makeQuery(id+"F15.opExtrude","SWEPT_EDGE",EDGE,{"disambiguationData":[OSD([sQuery(id+"F12.wireOp",EDGE,"E18"),sQuery(id+"F12.wireOp",EDGE,"E35")])]});
            var Q7;
            Q7=makeQuery(id+"F15.opExtrude","SWEPT_EDGE",EDGE,{"disambiguationData":[OSD([sQuery(id+"F12.wireOp",EDGE,"E18"),sQuery(id+"F12.wireOp",EDGE,"E32")])]});
            fillet(context, id + "F16", {"entities" : qUnion([Q0, Q1, Q2, Q3, Q4, Q5, Q6, Q7]), "radius" : 5 * mm, "tangentPropagation" : true, "allowEdgeOverflow" : false});
        }
        {
            var Q0;
            Q0=makeQuery(id+"F12.imprint","IMPRINT",FACE,{"disambiguationData":[TD([[makeQuery(id+"F12.imprint","IMPRINT",EDGE,{"derivedFrom":sQuery(id+"F12.wireOp",EDGE,"E13")}),-1.0]])]});
            var sketch = newSketch(context, id + "F17", { "sketchPlane" : qUnion([Q0])});
            skCircle(sketch, "E45", {"center": v(0, 0) * mm, "radius": 9 * mm});
            skCircle(sketch, "E46", {"center": v(0, 0) * mm, "radius": 11.1 * mm});
            skCircle(sketch, "E47", {"center": v(0, 0) * mm, "radius": 16 * mm});
            skCircle(sketch, "E48.0", {"center": v(-61, 61) * mm, "radius": 7 * mm});
            skCircle(sketch, "E48.1", {"center": v(61, 61) * mm, "radius": 7 * mm});
            skCircle(sketch, "E48.2", {"center": v(-61, -61) * mm, "radius": 7 * mm});
            skCircle(sketch, "E48.3", {"center": v(61, -61) * mm, "radius": 7 * mm});
            skLineSegment(sketch, "E49", {"start": v(-16, 0) * mm, "end": v(-66.23, 56.34) * mm});
            skLineSegment(sketch, "E50", {"start": v(0, 16) * mm, "end": v(-56.34, 66.23) * mm});
            skLineSegment(sketch, "E51", {"start": v(0, 16) * mm, "end": v(56.34, 66.23) * mm});
            skLineSegment(sketch, "E52", {"start": v(16, 0) * mm, "end": v(66.23, 56.34) * mm});
            skLineSegment(sketch, "E53", {"start": v(16, 0) * mm, "end": v(66.23, -56.34) * mm});
            skLineSegment(sketch, "E54", {"start": v(0, -16) * mm, "end": v(56.34, -66.23) * mm});
            skLineSegment(sketch, "E55", {"start": v(0, -16) * mm, "end": v(-56.34, -66.23) * mm});
            skLineSegment(sketch, "E56", {"start": v(-16, 0) * mm, "end": v(-66.23, -56.34) * mm});
            skCircle(sketch, "E57.0", {"center": v(-61, 61) * mm, "radius": 2.5 * mm});
            skCircle(sketch, "E57.1", {"center": v(61, 61) * mm, "radius": 2.5 * mm});
            skCircle(sketch, "E57.2", {"center": v(-61, -61) * mm, "radius": 2.5 * mm});
            skCircle(sketch, "E57.3", {"center": v(61, -61) * mm, "radius": 2.5 * mm});
            skLineSegment(sketch, "E58.0", {"start": v(-16.06, -0.05) * mm, "end": v(-66.28, 56.3) * mm});
            skLineSegment(sketch, "E59.0", {"start": v(-15.76, 2.74) * mm, "end": v(-61.47, 54.02) * mm});
            skLineSegment(sketch, "E60.0", {"start": v(-2.74, 15.76) * mm, "end": v(-54.02, 61.47) * mm});
            skLineSegment(sketch, "E61.1.0", {"start": v(-15.76, -2.74) * mm, "end": v(-61.47, -54.02) * mm});
            skLineSegment(sketch, "E61.1.1", {"start": v(-2.74, -15.76) * mm, "end": v(-54.02, -61.47) * mm});
            skLineSegment(sketch, "E61.2.0", {"start": v(2.74, -15.76) * mm, "end": v(54.02, -61.47) * mm});
            skLineSegment(sketch, "E61.2.1", {"start": v(15.76, -2.74) * mm, "end": v(61.47, -54.02) * mm});
            skLineSegment(sketch, "E61.3.0", {"start": v(15.76, 2.74) * mm, "end": v(61.47, 54.02) * mm});
            skLineSegment(sketch, "E61.3.1", {"start": v(2.74, 15.76) * mm, "end": v(54.02, 61.47) * mm});
            skLineSegment(sketch, "E62", {"start": v(28.17, 41.11) * mm, "end": v(41.11, 28.17) * mm});
            skLineSegment(sketch, "E63.1.0", {"start": v(-41.11, 28.17) * mm, "end": v(-28.17, 41.11) * mm});
            skLineSegment(sketch, "E63.2.0", {"start": v(-28.17, -41.11) * mm, "end": v(-41.11, -28.17) * mm});
            skLineSegment(sketch, "E63.3.0", {"start": v(41.11, -28.17) * mm, "end": v(28.17, -41.11) * mm});
            skSolve(sketch);
        }
        {
            var Q0;
            Q0=makeQuery(id+"F17.imprint","IMPRINT",FACE,{"disambiguationData":[TD([[makeQuery(id+"F17.imprint","IMPRINT",EDGE,{"derivedFrom":sQuery(id+"F17.wireOp",EDGE,"E46")}),-1.0]])]});
            var Q1;
            {var subQ1=sQuery(id+"F17.wireOp",EDGE,"E47");var subQ3=sQuery(id+"F17.wireOp",EDGE,"E61.3.0");var subQ4=makeQuery(id+"F17.imprint","INTERSECT",VERTEX,{"derivedFrom":[subQ1,subQ3]});Q1=makeQuery(id+"F17.imprint","IMPRINT",FACE,{"disambiguationData":[TD([[makeQuery(id+"F17.imprint","IMPRINT",EDGE,{"disambiguationData":[TD([[subQ4,-1.0]])],"derivedFrom":subQ3}),-1.0]])]});}
            var Q2;
            {var subQ0=sQuery(id+"F17.wireOp",EDGE,"E61.3.0");var subQ1=sQuery(id+"F17.wireOp",EDGE,"E47");var subQ2=makeQuery(id+"F17.imprint","INTERSECT",VERTEX,{"derivedFrom":[subQ1,subQ0]});Q2=makeQuery(id+"F17.imprint","IMPRINT",FACE,{"disambiguationData":[TD([[makeQuery(id+"F17.imprint","IMPRINT",EDGE,{"disambiguationData":[TD([[subQ2,-1.0]])],"derivedFrom":subQ1}),-1.0]])]});}
            var Q3;
            {var subQ1=sQuery(id+"F17.wireOp",EDGE,"E47");var subQ3=sQuery(id+"F17.wireOp",EDGE,"E61.3.1");var subQ4=makeQuery(id+"F17.imprint","INTERSECT",VERTEX,{"derivedFrom":[subQ1,subQ3]});Q3=makeQuery(id+"F17.imprint","IMPRINT",FACE,{"disambiguationData":[TD([[makeQuery(id+"F17.imprint","IMPRINT",EDGE,{"disambiguationData":[TD([[subQ4,-1.0]])],"derivedFrom":subQ3}),1.0]])]});}
            var Q4;
            {var subQ1=sQuery(id+"F17.wireOp",EDGE,"E47");var subQ3=sQuery(id+"F17.wireOp",EDGE,"E60.0");var subQ4=makeQuery(id+"F17.imprint","INTERSECT",VERTEX,{"derivedFrom":[subQ1,subQ3]});Q4=makeQuery(id+"F17.imprint","IMPRINT",FACE,{"disambiguationData":[TD([[makeQuery(id+"F17.imprint","IMPRINT",EDGE,{"disambiguationData":[TD([[subQ4,-1.0]])],"derivedFrom":subQ3}),-1.0]])]});}
            var Q5;
            {var subQ0=sQuery(id+"F17.wireOp",EDGE,"E59.0");var subQ1=sQuery(id+"F17.wireOp",EDGE,"E47");var subQ2=makeQuery(id+"F17.imprint","INTERSECT",VERTEX,{"derivedFrom":[subQ1,subQ0]});Q5=makeQuery(id+"F17.imprint","IMPRINT",FACE,{"disambiguationData":[TD([[makeQuery(id+"F17.imprint","IMPRINT",EDGE,{"disambiguationData":[TD([[subQ2,1.0]])],"derivedFrom":subQ1}),-1.0]])]});}
            var Q6;
            {var subQ1=sQuery(id+"F17.wireOp",EDGE,"E47");var subQ3=sQuery(id+"F17.wireOp",EDGE,"E59.0");var subQ4=makeQuery(id+"F17.imprint","INTERSECT",VERTEX,{"derivedFrom":[subQ1,subQ3]});Q6=makeQuery(id+"F17.imprint","IMPRINT",FACE,{"disambiguationData":[TD([[makeQuery(id+"F17.imprint","IMPRINT",EDGE,{"disambiguationData":[TD([[subQ4,-1.0]])],"derivedFrom":subQ3}),1.0]])]});}
            var Q7;
            {var subQ1=sQuery(id+"F17.wireOp",EDGE,"E47");var subQ3=sQuery(id+"F17.wireOp",EDGE,"E61.1.0");var subQ4=makeQuery(id+"F17.imprint","INTERSECT",VERTEX,{"derivedFrom":[subQ1,subQ3]});Q7=makeQuery(id+"F17.imprint","IMPRINT",FACE,{"disambiguationData":[TD([[makeQuery(id+"F17.imprint","IMPRINT",EDGE,{"disambiguationData":[TD([[subQ4,-1.0]])],"derivedFrom":subQ3}),-1.0]])]});}
            var Q8;
            {var subQ0=sQuery(id+"F17.wireOp",EDGE,"E61.1.0");var subQ1=sQuery(id+"F17.wireOp",EDGE,"E47");var subQ2=makeQuery(id+"F17.imprint","INTERSECT",VERTEX,{"derivedFrom":[subQ1,subQ0]});Q8=makeQuery(id+"F17.imprint","IMPRINT",FACE,{"disambiguationData":[TD([[makeQuery(id+"F17.imprint","IMPRINT",EDGE,{"disambiguationData":[TD([[subQ2,-1.0]])],"derivedFrom":subQ1}),-1.0]])]});}
            var Q9;
            {var subQ1=sQuery(id+"F17.wireOp",EDGE,"E47");var subQ3=sQuery(id+"F17.wireOp",EDGE,"E61.1.1");var subQ4=makeQuery(id+"F17.imprint","INTERSECT",VERTEX,{"derivedFrom":[subQ1,subQ3]});Q9=makeQuery(id+"F17.imprint","IMPRINT",FACE,{"disambiguationData":[TD([[makeQuery(id+"F17.imprint","IMPRINT",EDGE,{"disambiguationData":[TD([[subQ4,-1.0]])],"derivedFrom":subQ3}),1.0]])]});}
            var Q10;
            {var subQ1=sQuery(id+"F17.wireOp",EDGE,"E47");var subQ3=sQuery(id+"F17.wireOp",EDGE,"E61.2.0");var subQ4=makeQuery(id+"F17.imprint","INTERSECT",VERTEX,{"derivedFrom":[subQ1,subQ3]});Q10=makeQuery(id+"F17.imprint","IMPRINT",FACE,{"disambiguationData":[TD([[makeQuery(id+"F17.imprint","IMPRINT",EDGE,{"disambiguationData":[TD([[subQ4,-1.0]])],"derivedFrom":subQ3}),-1.0]])]});}
            var Q11;
            {var subQ0=sQuery(id+"F17.wireOp",EDGE,"E61.2.0");var subQ1=sQuery(id+"F17.wireOp",EDGE,"E47");var subQ2=makeQuery(id+"F17.imprint","INTERSECT",VERTEX,{"derivedFrom":[subQ1,subQ0]});Q11=makeQuery(id+"F17.imprint","IMPRINT",FACE,{"disambiguationData":[TD([[makeQuery(id+"F17.imprint","IMPRINT",EDGE,{"disambiguationData":[TD([[subQ2,-1.0]])],"derivedFrom":subQ1}),-1.0]])]});}
            var Q12;
            {var subQ1=sQuery(id+"F17.wireOp",EDGE,"E47");var subQ3=sQuery(id+"F17.wireOp",EDGE,"E61.2.1");var subQ4=makeQuery(id+"F17.imprint","INTERSECT",VERTEX,{"derivedFrom":[subQ1,subQ3]});Q12=makeQuery(id+"F17.imprint","IMPRINT",FACE,{"disambiguationData":[TD([[makeQuery(id+"F17.imprint","IMPRINT",EDGE,{"disambiguationData":[TD([[subQ4,-1.0]])],"derivedFrom":subQ3}),1.0]])]});}
            extrude(context, id + "F18", {"entities" : qUnion([Q0, Q1, Q2, Q3, Q4, Q5, Q6, Q7, Q8, Q9, Q10, Q11, Q12]), "depth" : 15 * mm, "offsetDistance" : 25 * mm});
        }
        {
            var Q0;
            {var subQ0=sQuery(id+"F17.wireOp",EDGE,"E59.0");var subQ1=sQuery(id+"F17.wireOp",EDGE,"E47");var subQ2=makeQuery(id+"F17.imprint","INTERSECT",VERTEX,{"derivedFrom":[subQ1,subQ0]});Q0=makeQuery(id+"F17.imprint","IMPRINT",FACE,{"disambiguationData":[TD([[makeQuery(id+"F17.imprint","IMPRINT",EDGE,{"disambiguationData":[TD([[subQ2,1.0]])],"derivedFrom":subQ1}),-1.0]])]});}
            var Q1;
            {var subQ0=sQuery(id+"F12.wireOp",EDGE,"E44.1.0");var subQ2=sQuery(id+"F12.wireOp",EDGE,"E43");var subQ3=makeQuery(id+"F12.imprint","INTERSECT",VERTEX,{"disambiguationData":[OD(0.0)],"derivedFrom":[subQ2,subQ0]});var subQ6=makeQuery(id+"F12.imprint","IMPRINT",EDGE,{"disambiguationData":[TD([[subQ3,-1.0]])],"derivedFrom":subQ2});Q1=makeQuery(id+"F17.imprint","IMPRINT",FACE,{"disambiguationData":[TD([[makeQuery(id+"F17.imprint","IMPRINT",EDGE,{"derivedFrom":subQ6}),-1.0]])]});}
            var Q2;
            {var subQ6=sQuery(id+"F17.wireOp",EDGE,"E48.0");var subQ11=sQuery(id+"F17.wireOp",EDGE,"E59.0");var subQ12=makeQuery(id+"F17.imprint","INTERSECT",VERTEX,{"derivedFrom":[subQ6,subQ11]});Q2=makeQuery(id+"F17.imprint","IMPRINT",FACE,{"disambiguationData":[TD([[makeQuery(id+"F17.imprint","IMPRINT",EDGE,{"disambiguationData":[TD([[subQ12,-1.0]])],"derivedFrom":subQ6}),-1.0]])]});}
            var Q3;
            {var subQ0=sQuery(id+"F17.wireOp",EDGE,"E61.2.0");var subQ1=sQuery(id+"F17.wireOp",EDGE,"E47");var subQ2=makeQuery(id+"F17.imprint","INTERSECT",VERTEX,{"derivedFrom":[subQ1,subQ0]});Q3=makeQuery(id+"F17.imprint","IMPRINT",FACE,{"disambiguationData":[TD([[makeQuery(id+"F17.imprint","IMPRINT",EDGE,{"disambiguationData":[TD([[subQ2,-1.0]])],"derivedFrom":subQ1}),-1.0]])]});}
            var Q4;
            {var subQ0=sQuery(id+"F17.wireOp",EDGE,"E61.2.0");var subQ1=makeQuery(id+"F12.imprint","IMPRINT",EDGE,{"derivedFrom":sQuery(id+"F12.wireOp",EDGE,"E13")});var subQ2=makeQuery(id+"F17.imprint","INTERSECT",VERTEX,{"derivedFrom":[subQ1,subQ0]});Q4=makeQuery(id+"F17.imprint","IMPRINT",FACE,{"disambiguationData":[TD([[makeQuery(id+"F17.imprint","IMPRINT",EDGE,{"disambiguationData":[TD([[subQ2,-1.0]])],"derivedFrom":subQ1}),-1.0]])]});}
            var Q5;
            {var subQ0=sQuery(id+"F17.wireOp",EDGE,"E61.2.0");var subQ1=sQuery(id+"F17.wireOp",EDGE,"E48.3");var subQ2=makeQuery(id+"F17.imprint","INTERSECT",VERTEX,{"derivedFrom":[subQ1,subQ0]});Q5=makeQuery(id+"F17.imprint","IMPRINT",FACE,{"disambiguationData":[TD([[makeQuery(id+"F17.imprint","IMPRINT",EDGE,{"disambiguationData":[TD([[subQ2,1.0]])],"derivedFrom":subQ1}),-1.0]])]});}
            var Q6;
            {var subQ0=sQuery(id+"F17.wireOp",EDGE,"E61.1.0");var subQ1=sQuery(id+"F17.wireOp",EDGE,"E47");var subQ2=makeQuery(id+"F17.imprint","INTERSECT",VERTEX,{"derivedFrom":[subQ1,subQ0]});Q6=makeQuery(id+"F17.imprint","IMPRINT",FACE,{"disambiguationData":[TD([[makeQuery(id+"F17.imprint","IMPRINT",EDGE,{"disambiguationData":[TD([[subQ2,-1.0]])],"derivedFrom":subQ1}),-1.0]])]});}
            var Q7;
            {var subQ0=sQuery(id+"F17.wireOp",EDGE,"E61.1.0");var subQ1=sQuery(id+"F17.wireOp",EDGE,"E48.2");var subQ2=makeQuery(id+"F17.imprint","INTERSECT",VERTEX,{"derivedFrom":[subQ1,subQ0]});Q7=makeQuery(id+"F17.imprint","IMPRINT",FACE,{"disambiguationData":[TD([[makeQuery(id+"F17.imprint","IMPRINT",EDGE,{"disambiguationData":[TD([[subQ2,1.0]])],"derivedFrom":subQ1}),-1.0]])]});}
            var Q8;
            {var subQ0=sQuery(id+"F17.wireOp",EDGE,"E61.1.0");var subQ1=makeQuery(id+"F12.imprint","IMPRINT",EDGE,{"derivedFrom":sQuery(id+"F12.wireOp",EDGE,"E13")});var subQ2=makeQuery(id+"F17.imprint","INTERSECT",VERTEX,{"derivedFrom":[subQ1,subQ0]});Q8=makeQuery(id+"F17.imprint","IMPRINT",FACE,{"disambiguationData":[TD([[makeQuery(id+"F17.imprint","IMPRINT",EDGE,{"disambiguationData":[TD([[subQ2,-1.0]])],"derivedFrom":subQ1}),-1.0]])]});}
            var Q9;
            {var subQ0=sQuery(id+"F17.wireOp",EDGE,"E61.3.0");var subQ1=sQuery(id+"F17.wireOp",EDGE,"E47");var subQ2=makeQuery(id+"F17.imprint","INTERSECT",VERTEX,{"derivedFrom":[subQ1,subQ0]});Q9=makeQuery(id+"F17.imprint","IMPRINT",FACE,{"disambiguationData":[TD([[makeQuery(id+"F17.imprint","IMPRINT",EDGE,{"disambiguationData":[TD([[subQ2,-1.0]])],"derivedFrom":subQ1}),-1.0]])]});}
            var Q10;
            {var subQ0=sQuery(id+"F17.wireOp",EDGE,"E61.3.0");var subQ1=makeQuery(id+"F12.imprint","IMPRINT",EDGE,{"derivedFrom":sQuery(id+"F12.wireOp",EDGE,"E13")});var subQ2=makeQuery(id+"F17.imprint","INTERSECT",VERTEX,{"derivedFrom":[subQ1,subQ0]});Q10=makeQuery(id+"F17.imprint","IMPRINT",FACE,{"disambiguationData":[TD([[makeQuery(id+"F17.imprint","IMPRINT",EDGE,{"disambiguationData":[TD([[subQ2,-1.0]])],"derivedFrom":subQ1}),-1.0]])]});}
            var Q11;
            {var subQ0=sQuery(id+"F17.wireOp",EDGE,"E61.3.0");var subQ1=sQuery(id+"F17.wireOp",EDGE,"E48.1");var subQ2=makeQuery(id+"F17.imprint","INTERSECT",VERTEX,{"derivedFrom":[subQ1,subQ0]});Q11=makeQuery(id+"F17.imprint","IMPRINT",FACE,{"disambiguationData":[TD([[makeQuery(id+"F17.imprint","IMPRINT",EDGE,{"disambiguationData":[TD([[subQ2,1.0]])],"derivedFrom":subQ1}),-1.0]])]});}
            var Q12;
            Q12=makeQuery(id+"F17.imprint","IMPRINT",FACE,{"disambiguationData":[TD([[makeQuery(id+"F17.imprint","IMPRINT",EDGE,{"derivedFrom":sQuery(id+"F17.wireOp",EDGE,"E45")}),-1.0]])]});
            var Q13;
            {var subQ0=sQuery(id+"F17.wireOp",EDGE,"E62");var subQ1=sQuery(id+"F17.wireOp",EDGE,"E61.3.0");var subQ2=makeQuery(id+"F17.imprint","INTERSECT",VERTEX,{"derivedFrom":[subQ1,subQ0]});Q13=makeQuery(id+"F17.imprint","IMPRINT",FACE,{"disambiguationData":[TD([[makeQuery(id+"F17.imprint","IMPRINT",EDGE,{"disambiguationData":[TD([[subQ2,-1.0]])],"derivedFrom":subQ1}),1.0]])]});}
            var Q14;
            Q14=makeQuery(id+"F17.imprint","IMPRINT",FACE,{"disambiguationData":[TD([[makeQuery(id+"F17.imprint","IMPRINT",EDGE,{"derivedFrom":sQuery(id+"F17.wireOp",EDGE,"E57.1")}),-1.0]])]});
            var Q15;
            {var subQ0=sQuery(id+"F17.wireOp",EDGE,"E62");var subQ1=sQuery(id+"F17.wireOp",EDGE,"E51");var subQ2=makeQuery(id+"F17.imprint","INTERSECT",VERTEX,{"derivedFrom":[subQ1,subQ0]});Q15=makeQuery(id+"F17.imprint","IMPRINT",FACE,{"disambiguationData":[TD([[makeQuery(id+"F17.imprint","IMPRINT",EDGE,{"disambiguationData":[TD([[subQ2,-1.0]])],"derivedFrom":subQ1}),-1.0]])]});}
            var Q16;
            {var subQ0=sQuery(id+"F17.wireOp",EDGE,"E51");var subQ5=makeQuery(id+"F12.imprint","IMPRINT",EDGE,{"derivedFrom":sQuery(id+"F12.wireOp",EDGE,"E13")});var subQ6=makeQuery(id+"F17.imprint","INTERSECT",VERTEX,{"derivedFrom":[subQ5,subQ0]});Q16=makeQuery(id+"F17.imprint","IMPRINT",FACE,{"disambiguationData":[TD([[makeQuery(id+"F17.imprint","IMPRINT",EDGE,{"disambiguationData":[TD([[subQ6,1.0]])],"derivedFrom":subQ5}),-1.0]])]});}
            var Q17;
            {var subQ0=sQuery(id+"F17.wireOp",EDGE,"E51");var subQ1=sQuery(id+"F17.wireOp",EDGE,"E48.1");var subQ2=makeQuery(id+"F17.imprint","INTERSECT",VERTEX,{"derivedFrom":[subQ1,subQ0]});Q17=makeQuery(id+"F17.imprint","IMPRINT",FACE,{"disambiguationData":[TD([[makeQuery(id+"F17.imprint","IMPRINT",EDGE,{"disambiguationData":[TD([[subQ2,-1.0]])],"derivedFrom":subQ1}),-1.0]])]});}
            var Q18;
            {var subQ0=sQuery(id+"F17.wireOp",EDGE,"E52");var subQ1=sQuery(id+"F17.wireOp",EDGE,"E48.1");var subQ2=makeQuery(id+"F17.imprint","INTERSECT",VERTEX,{"derivedFrom":[subQ1,subQ0]});Q18=makeQuery(id+"F17.imprint","IMPRINT",FACE,{"disambiguationData":[TD([[makeQuery(id+"F17.imprint","IMPRINT",EDGE,{"disambiguationData":[TD([[subQ2,1.0]])],"derivedFrom":subQ1}),-1.0]])]});}
            var Q19;
            {var subQ0=sQuery(id+"F17.wireOp",EDGE,"E52");var subQ5=makeQuery(id+"F12.imprint","IMPRINT",EDGE,{"derivedFrom":sQuery(id+"F12.wireOp",EDGE,"E13")});var subQ6=makeQuery(id+"F17.imprint","INTERSECT",VERTEX,{"derivedFrom":[subQ5,subQ0]});Q19=makeQuery(id+"F17.imprint","IMPRINT",FACE,{"disambiguationData":[TD([[makeQuery(id+"F17.imprint","IMPRINT",EDGE,{"disambiguationData":[TD([[subQ6,-1.0]])],"derivedFrom":subQ5}),-1.0]])]});}
            var Q20;
            {var subQ0=sQuery(id+"F17.wireOp",EDGE,"E62");var subQ1=sQuery(id+"F17.wireOp",EDGE,"E52");var subQ2=makeQuery(id+"F17.imprint","INTERSECT",VERTEX,{"derivedFrom":[subQ1,subQ0]});Q20=makeQuery(id+"F17.imprint","IMPRINT",FACE,{"disambiguationData":[TD([[makeQuery(id+"F17.imprint","IMPRINT",EDGE,{"disambiguationData":[TD([[subQ2,-1.0]])],"derivedFrom":subQ1}),1.0]])]});}
            var Q21;
            {var subQ0=sQuery(id+"F17.wireOp",EDGE,"E63.2.0");var subQ1=sQuery(id+"F17.wireOp",EDGE,"E55");var subQ2=makeQuery(id+"F17.imprint","INTERSECT",VERTEX,{"derivedFrom":[subQ1,subQ0]});Q21=makeQuery(id+"F17.imprint","IMPRINT",FACE,{"disambiguationData":[TD([[makeQuery(id+"F17.imprint","IMPRINT",EDGE,{"disambiguationData":[TD([[subQ2,-1.0]])],"derivedFrom":subQ1}),-1.0]])]});}
            var Q22;
            {var subQ0=sQuery(id+"F17.wireOp",EDGE,"E63.2.0");var subQ1=sQuery(id+"F17.wireOp",EDGE,"E61.1.0");var subQ2=makeQuery(id+"F17.imprint","INTERSECT",VERTEX,{"derivedFrom":[subQ1,subQ0]});Q22=makeQuery(id+"F17.imprint","IMPRINT",FACE,{"disambiguationData":[TD([[makeQuery(id+"F17.imprint","IMPRINT",EDGE,{"disambiguationData":[TD([[subQ2,-1.0]])],"derivedFrom":subQ1}),1.0]])]});}
            var Q23;
            {var subQ0=sQuery(id+"F17.wireOp",EDGE,"E63.2.0");var subQ1=sQuery(id+"F17.wireOp",EDGE,"E56");var subQ2=makeQuery(id+"F17.imprint","INTERSECT",VERTEX,{"derivedFrom":[subQ1,subQ0]});Q23=makeQuery(id+"F17.imprint","IMPRINT",FACE,{"disambiguationData":[TD([[makeQuery(id+"F17.imprint","IMPRINT",EDGE,{"disambiguationData":[TD([[subQ2,-1.0]])],"derivedFrom":subQ1}),1.0]])]});}
            var Q24;
            {var subQ0=sQuery(id+"F17.wireOp",EDGE,"E56");var subQ5=makeQuery(id+"F12.imprint","IMPRINT",EDGE,{"derivedFrom":sQuery(id+"F12.wireOp",EDGE,"E13")});var subQ6=makeQuery(id+"F17.imprint","INTERSECT",VERTEX,{"derivedFrom":[subQ5,subQ0]});Q24=makeQuery(id+"F17.imprint","IMPRINT",FACE,{"disambiguationData":[TD([[makeQuery(id+"F17.imprint","IMPRINT",EDGE,{"disambiguationData":[TD([[subQ6,-1.0]])],"derivedFrom":subQ5}),-1.0]])]});}
            var Q25;
            Q25=makeQuery(id+"F17.imprint","IMPRINT",FACE,{"disambiguationData":[TD([[makeQuery(id+"F17.imprint","IMPRINT",EDGE,{"derivedFrom":sQuery(id+"F17.wireOp",EDGE,"E57.2")}),-1.0]])]});
            var Q26;
            {var subQ0=sQuery(id+"F17.wireOp",EDGE,"E55");var subQ1=sQuery(id+"F17.wireOp",EDGE,"E48.2");var subQ2=makeQuery(id+"F17.imprint","INTERSECT",VERTEX,{"derivedFrom":[subQ1,subQ0]});Q26=makeQuery(id+"F17.imprint","IMPRINT",FACE,{"disambiguationData":[TD([[makeQuery(id+"F17.imprint","IMPRINT",EDGE,{"disambiguationData":[TD([[subQ2,-1.0]])],"derivedFrom":subQ1}),-1.0]])]});}
            var Q27;
            {var subQ0=sQuery(id+"F17.wireOp",EDGE,"E55");var subQ5=makeQuery(id+"F12.imprint","IMPRINT",EDGE,{"derivedFrom":sQuery(id+"F12.wireOp",EDGE,"E13")});var subQ6=makeQuery(id+"F17.imprint","INTERSECT",VERTEX,{"derivedFrom":[subQ5,subQ0]});Q27=makeQuery(id+"F17.imprint","IMPRINT",FACE,{"disambiguationData":[TD([[makeQuery(id+"F17.imprint","IMPRINT",EDGE,{"disambiguationData":[TD([[subQ6,1.0]])],"derivedFrom":subQ5}),-1.0]])]});}
            var Q28;
            {var subQ0=sQuery(id+"F17.wireOp",EDGE,"E56");var subQ1=sQuery(id+"F17.wireOp",EDGE,"E48.2");var subQ2=makeQuery(id+"F17.imprint","INTERSECT",VERTEX,{"derivedFrom":[subQ1,subQ0]});Q28=makeQuery(id+"F17.imprint","IMPRINT",FACE,{"disambiguationData":[TD([[makeQuery(id+"F17.imprint","IMPRINT",EDGE,{"disambiguationData":[TD([[subQ2,1.0]])],"derivedFrom":subQ1}),-1.0]])]});}
            var Q29;
            {var subQ0=sQuery(id+"F17.wireOp",EDGE,"E63.3.0");var subQ1=sQuery(id+"F17.wireOp",EDGE,"E54");var subQ2=makeQuery(id+"F17.imprint","INTERSECT",VERTEX,{"derivedFrom":[subQ1,subQ0]});Q29=makeQuery(id+"F17.imprint","IMPRINT",FACE,{"disambiguationData":[TD([[makeQuery(id+"F17.imprint","IMPRINT",EDGE,{"disambiguationData":[TD([[subQ2,-1.0]])],"derivedFrom":subQ1}),1.0]])]});}
            var Q30;
            {var subQ0=sQuery(id+"F17.wireOp",EDGE,"E63.3.0");var subQ1=sQuery(id+"F17.wireOp",EDGE,"E61.2.0");var subQ2=makeQuery(id+"F17.imprint","INTERSECT",VERTEX,{"derivedFrom":[subQ1,subQ0]});Q30=makeQuery(id+"F17.imprint","IMPRINT",FACE,{"disambiguationData":[TD([[makeQuery(id+"F17.imprint","IMPRINT",EDGE,{"disambiguationData":[TD([[subQ2,-1.0]])],"derivedFrom":subQ1}),1.0]])]});}
            var Q31;
            {var subQ0=sQuery(id+"F17.wireOp",EDGE,"E63.3.0");var subQ1=sQuery(id+"F17.wireOp",EDGE,"E53");var subQ2=makeQuery(id+"F17.imprint","INTERSECT",VERTEX,{"derivedFrom":[subQ1,subQ0]});Q31=makeQuery(id+"F17.imprint","IMPRINT",FACE,{"disambiguationData":[TD([[makeQuery(id+"F17.imprint","IMPRINT",EDGE,{"disambiguationData":[TD([[subQ2,-1.0]])],"derivedFrom":subQ1}),-1.0]])]});}
            var Q32;
            {var subQ0=sQuery(id+"F17.wireOp",EDGE,"E53");var subQ5=makeQuery(id+"F12.imprint","IMPRINT",EDGE,{"derivedFrom":sQuery(id+"F12.wireOp",EDGE,"E13")});var subQ6=makeQuery(id+"F17.imprint","INTERSECT",VERTEX,{"derivedFrom":[subQ5,subQ0]});Q32=makeQuery(id+"F17.imprint","IMPRINT",FACE,{"disambiguationData":[TD([[makeQuery(id+"F17.imprint","IMPRINT",EDGE,{"disambiguationData":[TD([[subQ6,1.0]])],"derivedFrom":subQ5}),-1.0]])]});}
            var Q33;
            {var subQ0=sQuery(id+"F17.wireOp",EDGE,"E53");var subQ1=sQuery(id+"F17.wireOp",EDGE,"E48.3");var subQ2=makeQuery(id+"F17.imprint","INTERSECT",VERTEX,{"derivedFrom":[subQ1,subQ0]});Q33=makeQuery(id+"F17.imprint","IMPRINT",FACE,{"disambiguationData":[TD([[makeQuery(id+"F17.imprint","IMPRINT",EDGE,{"disambiguationData":[TD([[subQ2,-1.0]])],"derivedFrom":subQ1}),-1.0]])]});}
            var Q34;
            {var subQ0=sQuery(id+"F17.wireOp",EDGE,"E54");var subQ1=sQuery(id+"F17.wireOp",EDGE,"E48.3");var subQ2=makeQuery(id+"F17.imprint","INTERSECT",VERTEX,{"derivedFrom":[subQ1,subQ0]});Q34=makeQuery(id+"F17.imprint","IMPRINT",FACE,{"disambiguationData":[TD([[makeQuery(id+"F17.imprint","IMPRINT",EDGE,{"disambiguationData":[TD([[subQ2,1.0]])],"derivedFrom":subQ1}),-1.0]])]});}
            var Q35;
            {var subQ0=sQuery(id+"F17.wireOp",EDGE,"E54");var subQ5=makeQuery(id+"F12.imprint","IMPRINT",EDGE,{"derivedFrom":sQuery(id+"F12.wireOp",EDGE,"E13")});var subQ6=makeQuery(id+"F17.imprint","INTERSECT",VERTEX,{"derivedFrom":[subQ5,subQ0]});Q35=makeQuery(id+"F17.imprint","IMPRINT",FACE,{"disambiguationData":[TD([[makeQuery(id+"F17.imprint","IMPRINT",EDGE,{"disambiguationData":[TD([[subQ6,-1.0]])],"derivedFrom":subQ5}),-1.0]])]});}
            var Q36;
            Q36=makeQuery(id+"F17.imprint","IMPRINT",FACE,{"disambiguationData":[TD([[makeQuery(id+"F17.imprint","IMPRINT",EDGE,{"derivedFrom":sQuery(id+"F17.wireOp",EDGE,"E57.3")}),-1.0]])]});
            var Q37;
            {var subQ0=sQuery(id+"F17.wireOp",EDGE,"E63.1.0");var subQ1=sQuery(id+"F17.wireOp",EDGE,"E59.0");var subQ2=makeQuery(id+"F17.imprint","INTERSECT",VERTEX,{"derivedFrom":[subQ1,subQ0]});Q37=makeQuery(id+"F17.imprint","IMPRINT",FACE,{"disambiguationData":[TD([[makeQuery(id+"F17.imprint","IMPRINT",EDGE,{"disambiguationData":[TD([[subQ2,-1.0]])],"derivedFrom":subQ1}),-1.0]])]});}
            var Q38;
            {var subQ0=sQuery(id+"F17.wireOp",EDGE,"E63.1.0");var subQ1=sQuery(id+"F17.wireOp",EDGE,"E50");var subQ2=makeQuery(id+"F17.imprint","INTERSECT",VERTEX,{"derivedFrom":[subQ1,subQ0]});Q38=makeQuery(id+"F17.imprint","IMPRINT",FACE,{"disambiguationData":[TD([[makeQuery(id+"F17.imprint","IMPRINT",EDGE,{"disambiguationData":[TD([[subQ2,-1.0]])],"derivedFrom":subQ1}),1.0]])]});}
            var Q39;
            {var subQ0=sQuery(id+"F17.wireOp",EDGE,"E50");var subQ4=makeQuery(id+"F12.imprint","IMPRINT",EDGE,{"derivedFrom":sQuery(id+"F12.wireOp",EDGE,"E13")});var subQ5=makeQuery(id+"F17.imprint","INTERSECT",VERTEX,{"derivedFrom":[subQ4,subQ0]});Q39=makeQuery(id+"F17.imprint","IMPRINT",FACE,{"disambiguationData":[TD([[makeQuery(id+"F17.imprint","IMPRINT",EDGE,{"disambiguationData":[TD([[subQ5,-1.0]])],"derivedFrom":subQ4}),-1.0]])]});}
            var Q40;
            {var subQ0=sQuery(id+"F17.wireOp",EDGE,"E50");var subQ1=sQuery(id+"F17.wireOp",EDGE,"E48.0");var subQ2=makeQuery(id+"F17.imprint","INTERSECT",VERTEX,{"derivedFrom":[subQ1,subQ0]});Q40=makeQuery(id+"F17.imprint","IMPRINT",FACE,{"disambiguationData":[TD([[makeQuery(id+"F17.imprint","IMPRINT",EDGE,{"disambiguationData":[TD([[subQ2,1.0]])],"derivedFrom":subQ1}),-1.0]])]});}
            var Q41;
            Q41=makeQuery(id+"F17.imprint","IMPRINT",FACE,{"disambiguationData":[TD([[makeQuery(id+"F17.imprint","IMPRINT",EDGE,{"derivedFrom":sQuery(id+"F17.wireOp",EDGE,"E57.0")}),-1.0]])]});
            var Q42;
            {var subQ0=sQuery(id+"F17.wireOp",EDGE,"E49");var subQ1=sQuery(id+"F17.wireOp",EDGE,"E48.0");var subQ2=makeQuery(id+"F17.imprint","INTERSECT",VERTEX,{"derivedFrom":[subQ1,subQ0]});Q42=makeQuery(id+"F17.imprint","IMPRINT",FACE,{"disambiguationData":[TD([[makeQuery(id+"F17.imprint","IMPRINT",EDGE,{"disambiguationData":[TD([[subQ2,-1.0]])],"derivedFrom":subQ1}),-1.0]])]});}
            var Q43;
            {var subQ0=sQuery(id+"F17.wireOp",EDGE,"E63.1.0");var subQ1=sQuery(id+"F17.wireOp",EDGE,"E49");var subQ2=makeQuery(id+"F17.imprint","INTERSECT",VERTEX,{"derivedFrom":[subQ1,subQ0]});Q43=makeQuery(id+"F17.imprint","IMPRINT",FACE,{"disambiguationData":[TD([[makeQuery(id+"F17.imprint","IMPRINT",EDGE,{"disambiguationData":[TD([[subQ2,-1.0]])],"derivedFrom":subQ1}),-1.0]])]});}
            var Q44;
            {var subQ0=sQuery(id+"F17.wireOp",EDGE,"E49");var subQ4=makeQuery(id+"F12.imprint","IMPRINT",EDGE,{"derivedFrom":sQuery(id+"F12.wireOp",EDGE,"E13")});var subQ5=makeQuery(id+"F17.imprint","INTERSECT",VERTEX,{"derivedFrom":[subQ4,subQ0]});Q44=makeQuery(id+"F17.imprint","IMPRINT",FACE,{"disambiguationData":[TD([[makeQuery(id+"F17.imprint","IMPRINT",EDGE,{"disambiguationData":[TD([[subQ5,1.0]])],"derivedFrom":subQ4}),-1.0]])]});}
            extrude(context, id + "F19", {"entities" : qUnion([Q0, Q1, Q2, Q3, Q4, Q5, Q6, Q7, Q8, Q9, Q10, Q11, Q12, Q13, Q14, Q15, Q16, Q17, Q18, Q19, Q20, Q21, Q22, Q23, Q24, Q25, Q26, Q27, Q28, Q29, Q30, Q31, Q32, Q33, Q34, Q35, Q36, Q37, Q38, Q39, Q40, Q41, Q42, Q43, Q44]), "operationType" : NewBodyOperationType.ADD, "depth" : 3 * mm, "offsetDistance" : 25 * mm});
        }
        {
            var Q0;
            Q0=makeQuery(id+"F18.opExtrude","SWEPT_EDGE",EDGE,{"disambiguationData":[OSD([sQuery(id+"F17.wireOp",EDGE,"E47"),sQuery(id+"F17.wireOp",EDGE,"E61.3.1")])]});
            var Q1;
            Q1=makeQuery(id+"F18.opExtrude","SWEPT_EDGE",EDGE,{"disambiguationData":[OSD([sQuery(id+"F17.wireOp",EDGE,"E47"),sQuery(id+"F17.wireOp",EDGE,"E61.3.0")])]});
            var Q2;
            Q2=makeQuery(id+"F18.opExtrude","SWEPT_EDGE",EDGE,{"disambiguationData":[OSD([sQuery(id+"F17.wireOp",EDGE,"E47"),sQuery(id+"F17.wireOp",EDGE,"E60.0")])]});
            var Q3;
            Q3=makeQuery(id+"F18.opExtrude","SWEPT_EDGE",EDGE,{"disambiguationData":[OSD([sQuery(id+"F17.wireOp",EDGE,"E47"),sQuery(id+"F17.wireOp",EDGE,"E59.0")])]});
            var Q4;
            Q4=makeQuery(id+"F18.opExtrude","SWEPT_EDGE",EDGE,{"disambiguationData":[OSD([sQuery(id+"F17.wireOp",EDGE,"E47"),sQuery(id+"F17.wireOp",EDGE,"E61.1.0")])]});
            var Q5;
            Q5=makeQuery(id+"F18.opExtrude","SWEPT_EDGE",EDGE,{"disambiguationData":[OSD([sQuery(id+"F17.wireOp",EDGE,"E47"),sQuery(id+"F17.wireOp",EDGE,"E61.1.1")])]});
            var Q6;
            Q6=makeQuery(id+"F18.opExtrude","SWEPT_EDGE",EDGE,{"disambiguationData":[OSD([sQuery(id+"F17.wireOp",EDGE,"E47"),sQuery(id+"F17.wireOp",EDGE,"E61.2.1")])]});
            var Q7;
            Q7=makeQuery(id+"F18.opExtrude","SWEPT_EDGE",EDGE,{"disambiguationData":[OSD([sQuery(id+"F17.wireOp",EDGE,"E47"),sQuery(id+"F17.wireOp",EDGE,"E61.2.0")])]});
            var Q8;
            Q8=makeQuery(id+"F18.opExtrude","SWEPT_EDGE",EDGE,{"disambiguationData":[OSD([sQuery(id+"F17.wireOp",EDGE,"E48.0"),sQuery(id+"F17.wireOp",EDGE,"E60.0")])]});
            var Q9;
            Q9=makeQuery(id+"F18.opExtrude","SWEPT_EDGE",EDGE,{"disambiguationData":[OSD([sQuery(id+"F17.wireOp",EDGE,"E48.0"),sQuery(id+"F17.wireOp",EDGE,"E59.0")])]});
            var Q10;
            Q10=makeQuery(id+"F18.opExtrude","SWEPT_EDGE",EDGE,{"disambiguationData":[OSD([sQuery(id+"F17.wireOp",EDGE,"E48.3"),sQuery(id+"F17.wireOp",EDGE,"E61.2.0")])]});
            var Q11;
            Q11=makeQuery(id+"F18.opExtrude","SWEPT_EDGE",EDGE,{"disambiguationData":[OSD([sQuery(id+"F17.wireOp",EDGE,"E48.3"),sQuery(id+"F17.wireOp",EDGE,"E61.2.1")])]});
            var Q12;
            Q12=makeQuery(id+"F18.opExtrude","SWEPT_EDGE",EDGE,{"disambiguationData":[OSD([sQuery(id+"F17.wireOp",EDGE,"E48.2"),sQuery(id+"F17.wireOp",EDGE,"E61.1.0")])]});
            var Q13;
            Q13=makeQuery(id+"F18.opExtrude","SWEPT_EDGE",EDGE,{"disambiguationData":[OSD([sQuery(id+"F17.wireOp",EDGE,"E48.2"),sQuery(id+"F17.wireOp",EDGE,"E61.1.1")])]});
            var Q14;
            Q14=makeQuery(id+"F18.opExtrude","SWEPT_EDGE",EDGE,{"disambiguationData":[OSD([sQuery(id+"F17.wireOp",EDGE,"E48.1"),sQuery(id+"F17.wireOp",EDGE,"E61.3.1")])]});
            var Q15;
            Q15=makeQuery(id+"F18.opExtrude","SWEPT_EDGE",EDGE,{"disambiguationData":[OSD([sQuery(id+"F17.wireOp",EDGE,"E48.1"),sQuery(id+"F17.wireOp",EDGE,"E61.3.0")])]});
            var Q16;
            Q16=makeQuery(id+"F18.opExtrude","SWEPT_EDGE",EDGE,{"disambiguationData":[OSD([sQuery(id+"F17.wireOp",EDGE,"E47"),sQuery(id+"F17.wireOp",EDGE,"E54"),sQuery(id+"F17.wireOp",EDGE,"E55")])]});
            var Q17;
            Q17=makeQuery(id+"F18.opExtrude","SWEPT_EDGE",EDGE,{"disambiguationData":[OSD([sQuery(id+"F17.wireOp",EDGE,"E47"),sQuery(id+"F17.wireOp",EDGE,"E52"),sQuery(id+"F17.wireOp",EDGE,"E53")])]});
            var Q18;
            Q18=makeQuery(id+"F18.opExtrude","SWEPT_EDGE",EDGE,{"disambiguationData":[OSD([sQuery(id+"F17.wireOp",EDGE,"E47"),sQuery(id+"F17.wireOp",EDGE,"E50"),sQuery(id+"F17.wireOp",EDGE,"E51")])]});
            var Q19;
            Q19=makeQuery(id+"F18.opExtrude","SWEPT_EDGE",EDGE,{"disambiguationData":[OSD([sQuery(id+"F17.wireOp",EDGE,"E47"),sQuery(id+"F17.wireOp",EDGE,"E49"),sQuery(id+"F17.wireOp",EDGE,"E56")])]});
            fillet(context, id + "F20", {"entities" : qUnion([Q0, Q1, Q2, Q3, Q4, Q5, Q6, Q7, Q8, Q9, Q10, Q11, Q12, Q13, Q14, Q15, Q16, Q17, Q18, Q19]), "radius" : 5 * mm, "tangentPropagation" : true, "allowEdgeOverflow" : false});
        }
        {
            var Q0;
            Q0=makeQuery(id+"F18.opExtrude","CAP_EDGE",EDGE,{"disambiguationData":[OSD([sQuery(id+"F17.wireOp",EDGE,"E46")])],"isStart":false});
            chamfer(context, id + "F21", {"entities" : qUnion([Q0]), "chamferType" : ChamferType.TWO_OFFSETS, "width1" : 5 * mm, "oppositeDirection" : false, "width2" : 1 * mm, "tangentPropagation" : true});
        }
        {
            var Q0;
            {var subQ0=sQuery(id+"F17.wireOp",EDGE,"E62");Q0=makeQuery(id+"F19.boolean.opBoolean","MERGE",EDGE,{"derivedFrom":[makeQuery(id+"F19.opExtrude","CAP_EDGE",EDGE,{"disambiguationData":[OSD([subQ0]),TDD([makeQuery(id+"F17.imprint","IMPRINT",EDGE,{"disambiguationData":[TD([[makeQuery(id+"F17.imprint","INTERSECT",VERTEX,{"derivedFrom":[sQuery(id+"F17.wireOp",EDGE,"E51"),subQ0]}),-1.0]])],"derivedFrom":subQ0})])],"isStart":false}),makeQuery(id+"F19.opExtrude","CAP_EDGE",EDGE,{"disambiguationData":[OSD([subQ0]),TDD([makeQuery(id+"F17.imprint","IMPRINT",EDGE,{"disambiguationData":[TD([[makeQuery(id+"F17.imprint","INTERSECT",VERTEX,{"derivedFrom":[sQuery(id+"F17.wireOp",EDGE,"E52"),subQ0]}),1.0]])],"derivedFrom":subQ0})])],"isStart":false})]});}
            var Q1;
            {var subQ0=sQuery(id+"F17.wireOp",EDGE,"E63.1.0");Q1=makeQuery(id+"F19.boolean.opBoolean","MERGE",EDGE,{"derivedFrom":[makeQuery(id+"F19.opExtrude","CAP_EDGE",EDGE,{"disambiguationData":[OSD([subQ0]),TDD([makeQuery(id+"F17.imprint","IMPRINT",EDGE,{"disambiguationData":[TD([[makeQuery(id+"F17.imprint","INTERSECT",VERTEX,{"derivedFrom":[sQuery(id+"F17.wireOp",EDGE,"E49"),subQ0]}),-1.0]])],"derivedFrom":subQ0})])],"isStart":false}),makeQuery(id+"F19.opExtrude","CAP_EDGE",EDGE,{"disambiguationData":[OSD([subQ0]),TDD([makeQuery(id+"F17.imprint","IMPRINT",EDGE,{"disambiguationData":[TD([[makeQuery(id+"F17.imprint","INTERSECT",VERTEX,{"derivedFrom":[sQuery(id+"F17.wireOp",EDGE,"E50"),subQ0]}),1.0]])],"derivedFrom":subQ0})])],"isStart":false})]});}
            var Q2;
            {var subQ0=sQuery(id+"F17.wireOp",EDGE,"E63.2.0");Q2=makeQuery(id+"F19.boolean.opBoolean","MERGE",EDGE,{"derivedFrom":[makeQuery(id+"F19.opExtrude","CAP_EDGE",EDGE,{"disambiguationData":[OSD([subQ0]),TDD([makeQuery(id+"F17.imprint","IMPRINT",EDGE,{"disambiguationData":[TD([[makeQuery(id+"F17.imprint","INTERSECT",VERTEX,{"derivedFrom":[sQuery(id+"F17.wireOp",EDGE,"E55"),subQ0]}),-1.0]])],"derivedFrom":subQ0})])],"isStart":false}),makeQuery(id+"F19.opExtrude","CAP_EDGE",EDGE,{"disambiguationData":[OSD([subQ0]),TDD([makeQuery(id+"F17.imprint","IMPRINT",EDGE,{"disambiguationData":[TD([[makeQuery(id+"F17.imprint","INTERSECT",VERTEX,{"derivedFrom":[sQuery(id+"F17.wireOp",EDGE,"E56"),subQ0]}),1.0]])],"derivedFrom":subQ0})])],"isStart":false})]});}
            var Q3;
            {var subQ0=sQuery(id+"F17.wireOp",EDGE,"E63.3.0");Q3=makeQuery(id+"F19.boolean.opBoolean","MERGE",EDGE,{"derivedFrom":[makeQuery(id+"F19.opExtrude","CAP_EDGE",EDGE,{"disambiguationData":[OSD([subQ0]),TDD([makeQuery(id+"F17.imprint","IMPRINT",EDGE,{"disambiguationData":[TD([[makeQuery(id+"F17.imprint","INTERSECT",VERTEX,{"derivedFrom":[sQuery(id+"F17.wireOp",EDGE,"E53"),subQ0]}),-1.0]])],"derivedFrom":subQ0})])],"isStart":false}),makeQuery(id+"F19.opExtrude","CAP_EDGE",EDGE,{"disambiguationData":[OSD([subQ0]),TDD([makeQuery(id+"F17.imprint","IMPRINT",EDGE,{"disambiguationData":[TD([[makeQuery(id+"F17.imprint","INTERSECT",VERTEX,{"derivedFrom":[sQuery(id+"F17.wireOp",EDGE,"E54"),subQ0]}),1.0]])],"derivedFrom":subQ0})])],"isStart":false})]});}
            var Q4;
            Q4=makeQuery(id+"F18.opExtrude","CAP_EDGE",EDGE,{"disambiguationData":[OSD([sQuery(id+"F17.wireOp",EDGE,"E62")])],"isStart":false});
            var Q5;
            Q5=makeQuery(id+"F18.opExtrude","CAP_EDGE",EDGE,{"disambiguationData":[OSD([sQuery(id+"F17.wireOp",EDGE,"E63.3.0")])],"isStart":false});
            var Q6;
            Q6=makeQuery(id+"F18.opExtrude","CAP_EDGE",EDGE,{"disambiguationData":[OSD([sQuery(id+"F17.wireOp",EDGE,"E63.2.0")])],"isStart":false});
            var Q7;
            Q7=makeQuery(id+"F18.opExtrude","CAP_EDGE",EDGE,{"disambiguationData":[OSD([sQuery(id+"F17.wireOp",EDGE,"E63.1.0")])],"isStart":false});
            chamfer(context, id + "F22", {"entities" : qUnion([Q0, Q1, Q2, Q3, Q4, Q5, Q6, Q7]), "width" : 6 * mm, "tangentPropagation" : true});
        }
        {
            var Q0;
            {var subQ0=sQuery(id+"F17.wireOp",EDGE,"E62");var subQ1=sQuery(id+"F17.wireOp",EDGE,"E61.3.1");var subQ2=sQuery(id+"F17.wireOp",EDGE,"E61.3.0");var subQ3=sQuery(id+"F17.wireOp",EDGE,"E52");var subQ4=sQuery(id+"F17.wireOp",EDGE,"E51");Q0=makeQuery(id+"F22.opChamfer","BLEND_EDGE",EDGE,{"blendedFrom":[makeQuery(id+"F19.boolean.opBoolean","MERGE",EDGE,{"derivedFrom":[makeQuery(id+"F19.opExtrude","CAP_EDGE",EDGE,{"disambiguationData":[OSD([subQ0]),TDD([makeQuery(id+"F17.imprint","IMPRINT",EDGE,{"disambiguationData":[TD([[makeQuery(id+"F17.imprint","INTERSECT",VERTEX,{"derivedFrom":[subQ4,subQ0]}),-1.0]])],"derivedFrom":subQ0})])],"isStart":false}),makeQuery(id+"F19.opExtrude","CAP_EDGE",EDGE,{"disambiguationData":[OSD([subQ0]),TDD([makeQuery(id+"F17.imprint","IMPRINT",EDGE,{"disambiguationData":[TD([[makeQuery(id+"F17.imprint","INTERSECT",VERTEX,{"derivedFrom":[subQ3,subQ0]}),1.0]])],"derivedFrom":subQ0})])],"isStart":false})]}),makeQuery(id+"F19.opExtrude","CAP_FACE",FACE,{"disambiguationData":[OSD([sQuery(id+"F17.wireOp",EDGE,"E47"),sQuery(id+"F17.wireOp",EDGE,"E48.1"),subQ4,subQ3,sQuery(id+"F17.wireOp",EDGE,"E57.1"),subQ2,subQ1,subQ0])],"isStart":false})],"blendedInto":[makeQuery(id+"F19.opExtrude","CAP_FACE",FACE,{"disambiguationData":[OSD([sQuery(id+"F17.wireOp",EDGE,"E47"),sQuery(id+"F17.wireOp",EDGE,"E48.1"),subQ4,subQ3,sQuery(id+"F17.wireOp",EDGE,"E57.1"),subQ2,subQ1,subQ0])],"isStart":false})]});}
            var Q1;
            {var subQ0=sQuery(id+"F17.wireOp",EDGE,"E62");Q1=makeQuery(id+"F22.opChamfer","BLEND_EDGE",EDGE,{"blendedFrom":[makeQuery(id+"F18.opExtrude","CAP_EDGE",EDGE,{"disambiguationData":[OSD([subQ0])],"isStart":false}),makeQuery(id+"F18.opExtrude","CAP_FACE",FACE,{"disambiguationData":[OSD([sQuery(id+"F17.wireOp",EDGE,"E46"),sQuery(id+"F17.wireOp",EDGE,"E49"),sQuery(id+"F17.wireOp",EDGE,"E50"),sQuery(id+"F17.wireOp",EDGE,"E51"),sQuery(id+"F17.wireOp",EDGE,"E52"),sQuery(id+"F17.wireOp",EDGE,"E53"),sQuery(id+"F17.wireOp",EDGE,"E54"),sQuery(id+"F17.wireOp",EDGE,"E55"),sQuery(id+"F17.wireOp",EDGE,"E56"),subQ0,sQuery(id+"F17.wireOp",EDGE,"E63.1.0"),sQuery(id+"F17.wireOp",EDGE,"E63.2.0"),sQuery(id+"F17.wireOp",EDGE,"E63.3.0")])],"isStart":false})],"blendedInto":[makeQuery(id+"F18.opExtrude","CAP_FACE",FACE,{"disambiguationData":[OSD([sQuery(id+"F17.wireOp",EDGE,"E46"),sQuery(id+"F17.wireOp",EDGE,"E49"),sQuery(id+"F17.wireOp",EDGE,"E50"),sQuery(id+"F17.wireOp",EDGE,"E51"),sQuery(id+"F17.wireOp",EDGE,"E52"),sQuery(id+"F17.wireOp",EDGE,"E53"),sQuery(id+"F17.wireOp",EDGE,"E54"),sQuery(id+"F17.wireOp",EDGE,"E55"),sQuery(id+"F17.wireOp",EDGE,"E56"),subQ0,sQuery(id+"F17.wireOp",EDGE,"E63.1.0"),sQuery(id+"F17.wireOp",EDGE,"E63.2.0"),sQuery(id+"F17.wireOp",EDGE,"E63.3.0")])],"isStart":false})]});}
            var Q2;
            {var subQ0=sQuery(id+"F17.wireOp",EDGE,"E63.1.0");var subQ1=sQuery(id+"F17.wireOp",EDGE,"E60.0");var subQ2=sQuery(id+"F17.wireOp",EDGE,"E59.0");var subQ3=sQuery(id+"F17.wireOp",EDGE,"E50");var subQ4=sQuery(id+"F17.wireOp",EDGE,"E49");Q2=makeQuery(id+"F22.opChamfer","BLEND_EDGE",EDGE,{"blendedFrom":[makeQuery(id+"F19.boolean.opBoolean","MERGE",EDGE,{"derivedFrom":[makeQuery(id+"F19.opExtrude","CAP_EDGE",EDGE,{"disambiguationData":[OSD([subQ0]),TDD([makeQuery(id+"F17.imprint","IMPRINT",EDGE,{"disambiguationData":[TD([[makeQuery(id+"F17.imprint","INTERSECT",VERTEX,{"derivedFrom":[subQ4,subQ0]}),-1.0]])],"derivedFrom":subQ0})])],"isStart":false}),makeQuery(id+"F19.opExtrude","CAP_EDGE",EDGE,{"disambiguationData":[OSD([subQ0]),TDD([makeQuery(id+"F17.imprint","IMPRINT",EDGE,{"disambiguationData":[TD([[makeQuery(id+"F17.imprint","INTERSECT",VERTEX,{"derivedFrom":[subQ3,subQ0]}),1.0]])],"derivedFrom":subQ0})])],"isStart":false})]}),makeQuery(id+"F19.opExtrude","CAP_FACE",FACE,{"disambiguationData":[OSD([sQuery(id+"F17.wireOp",EDGE,"E47"),sQuery(id+"F17.wireOp",EDGE,"E48.0"),subQ4,subQ3,sQuery(id+"F17.wireOp",EDGE,"E57.0"),subQ2,subQ1,subQ0])],"isStart":false})],"blendedInto":[makeQuery(id+"F19.opExtrude","CAP_FACE",FACE,{"disambiguationData":[OSD([sQuery(id+"F17.wireOp",EDGE,"E47"),sQuery(id+"F17.wireOp",EDGE,"E48.0"),subQ4,subQ3,sQuery(id+"F17.wireOp",EDGE,"E57.0"),subQ2,subQ1,subQ0])],"isStart":false})]});}
            var Q3;
            {var subQ0=sQuery(id+"F17.wireOp",EDGE,"E63.1.0");Q3=makeQuery(id+"F22.opChamfer","BLEND_EDGE",EDGE,{"blendedFrom":[makeQuery(id+"F18.opExtrude","CAP_EDGE",EDGE,{"disambiguationData":[OSD([subQ0])],"isStart":false}),makeQuery(id+"F18.opExtrude","CAP_FACE",FACE,{"disambiguationData":[OSD([sQuery(id+"F17.wireOp",EDGE,"E46"),sQuery(id+"F17.wireOp",EDGE,"E49"),sQuery(id+"F17.wireOp",EDGE,"E50"),sQuery(id+"F17.wireOp",EDGE,"E51"),sQuery(id+"F17.wireOp",EDGE,"E52"),sQuery(id+"F17.wireOp",EDGE,"E53"),sQuery(id+"F17.wireOp",EDGE,"E54"),sQuery(id+"F17.wireOp",EDGE,"E55"),sQuery(id+"F17.wireOp",EDGE,"E56"),sQuery(id+"F17.wireOp",EDGE,"E62"),subQ0,sQuery(id+"F17.wireOp",EDGE,"E63.2.0"),sQuery(id+"F17.wireOp",EDGE,"E63.3.0")])],"isStart":false})],"blendedInto":[makeQuery(id+"F18.opExtrude","CAP_FACE",FACE,{"disambiguationData":[OSD([sQuery(id+"F17.wireOp",EDGE,"E46"),sQuery(id+"F17.wireOp",EDGE,"E49"),sQuery(id+"F17.wireOp",EDGE,"E50"),sQuery(id+"F17.wireOp",EDGE,"E51"),sQuery(id+"F17.wireOp",EDGE,"E52"),sQuery(id+"F17.wireOp",EDGE,"E53"),sQuery(id+"F17.wireOp",EDGE,"E54"),sQuery(id+"F17.wireOp",EDGE,"E55"),sQuery(id+"F17.wireOp",EDGE,"E56"),sQuery(id+"F17.wireOp",EDGE,"E62"),subQ0,sQuery(id+"F17.wireOp",EDGE,"E63.2.0"),sQuery(id+"F17.wireOp",EDGE,"E63.3.0")])],"isStart":false})]});}
            var Q4;
            {var subQ0=sQuery(id+"F17.wireOp",EDGE,"E63.3.0");var subQ1=sQuery(id+"F17.wireOp",EDGE,"E61.2.1");var subQ2=sQuery(id+"F17.wireOp",EDGE,"E61.2.0");var subQ3=sQuery(id+"F17.wireOp",EDGE,"E54");var subQ4=sQuery(id+"F17.wireOp",EDGE,"E53");Q4=makeQuery(id+"F22.opChamfer","BLEND_EDGE",EDGE,{"blendedFrom":[makeQuery(id+"F19.boolean.opBoolean","MERGE",EDGE,{"derivedFrom":[makeQuery(id+"F19.opExtrude","CAP_EDGE",EDGE,{"disambiguationData":[OSD([subQ0]),TDD([makeQuery(id+"F17.imprint","IMPRINT",EDGE,{"disambiguationData":[TD([[makeQuery(id+"F17.imprint","INTERSECT",VERTEX,{"derivedFrom":[subQ4,subQ0]}),-1.0]])],"derivedFrom":subQ0})])],"isStart":false}),makeQuery(id+"F19.opExtrude","CAP_EDGE",EDGE,{"disambiguationData":[OSD([subQ0]),TDD([makeQuery(id+"F17.imprint","IMPRINT",EDGE,{"disambiguationData":[TD([[makeQuery(id+"F17.imprint","INTERSECT",VERTEX,{"derivedFrom":[subQ3,subQ0]}),1.0]])],"derivedFrom":subQ0})])],"isStart":false})]}),makeQuery(id+"F19.opExtrude","CAP_FACE",FACE,{"disambiguationData":[OSD([sQuery(id+"F17.wireOp",EDGE,"E47"),sQuery(id+"F17.wireOp",EDGE,"E48.3"),subQ4,subQ3,sQuery(id+"F17.wireOp",EDGE,"E57.3"),subQ2,subQ1,subQ0])],"isStart":false})],"blendedInto":[makeQuery(id+"F19.opExtrude","CAP_FACE",FACE,{"disambiguationData":[OSD([sQuery(id+"F17.wireOp",EDGE,"E47"),sQuery(id+"F17.wireOp",EDGE,"E48.3"),subQ4,subQ3,sQuery(id+"F17.wireOp",EDGE,"E57.3"),subQ2,subQ1,subQ0])],"isStart":false})]});}
            var Q5;
            {var subQ0=sQuery(id+"F17.wireOp",EDGE,"E63.3.0");Q5=makeQuery(id+"F22.opChamfer","BLEND_EDGE",EDGE,{"blendedFrom":[makeQuery(id+"F18.opExtrude","CAP_EDGE",EDGE,{"disambiguationData":[OSD([subQ0])],"isStart":false}),makeQuery(id+"F18.opExtrude","CAP_FACE",FACE,{"disambiguationData":[OSD([sQuery(id+"F17.wireOp",EDGE,"E46"),sQuery(id+"F17.wireOp",EDGE,"E49"),sQuery(id+"F17.wireOp",EDGE,"E50"),sQuery(id+"F17.wireOp",EDGE,"E51"),sQuery(id+"F17.wireOp",EDGE,"E52"),sQuery(id+"F17.wireOp",EDGE,"E53"),sQuery(id+"F17.wireOp",EDGE,"E54"),sQuery(id+"F17.wireOp",EDGE,"E55"),sQuery(id+"F17.wireOp",EDGE,"E56"),sQuery(id+"F17.wireOp",EDGE,"E62"),sQuery(id+"F17.wireOp",EDGE,"E63.1.0"),sQuery(id+"F17.wireOp",EDGE,"E63.2.0"),subQ0])],"isStart":false})],"blendedInto":[makeQuery(id+"F18.opExtrude","CAP_FACE",FACE,{"disambiguationData":[OSD([sQuery(id+"F17.wireOp",EDGE,"E46"),sQuery(id+"F17.wireOp",EDGE,"E49"),sQuery(id+"F17.wireOp",EDGE,"E50"),sQuery(id+"F17.wireOp",EDGE,"E51"),sQuery(id+"F17.wireOp",EDGE,"E52"),sQuery(id+"F17.wireOp",EDGE,"E53"),sQuery(id+"F17.wireOp",EDGE,"E54"),sQuery(id+"F17.wireOp",EDGE,"E55"),sQuery(id+"F17.wireOp",EDGE,"E56"),sQuery(id+"F17.wireOp",EDGE,"E62"),sQuery(id+"F17.wireOp",EDGE,"E63.1.0"),sQuery(id+"F17.wireOp",EDGE,"E63.2.0"),subQ0])],"isStart":false})]});}
            var Q6;
            {var subQ0=sQuery(id+"F17.wireOp",EDGE,"E63.2.0");var subQ1=sQuery(id+"F17.wireOp",EDGE,"E61.1.1");var subQ2=sQuery(id+"F17.wireOp",EDGE,"E61.1.0");var subQ3=sQuery(id+"F17.wireOp",EDGE,"E56");var subQ4=sQuery(id+"F17.wireOp",EDGE,"E55");Q6=makeQuery(id+"F22.opChamfer","BLEND_EDGE",EDGE,{"blendedFrom":[makeQuery(id+"F19.boolean.opBoolean","MERGE",EDGE,{"derivedFrom":[makeQuery(id+"F19.opExtrude","CAP_EDGE",EDGE,{"disambiguationData":[OSD([subQ0]),TDD([makeQuery(id+"F17.imprint","IMPRINT",EDGE,{"disambiguationData":[TD([[makeQuery(id+"F17.imprint","INTERSECT",VERTEX,{"derivedFrom":[subQ4,subQ0]}),-1.0]])],"derivedFrom":subQ0})])],"isStart":false}),makeQuery(id+"F19.opExtrude","CAP_EDGE",EDGE,{"disambiguationData":[OSD([subQ0]),TDD([makeQuery(id+"F17.imprint","IMPRINT",EDGE,{"disambiguationData":[TD([[makeQuery(id+"F17.imprint","INTERSECT",VERTEX,{"derivedFrom":[subQ3,subQ0]}),1.0]])],"derivedFrom":subQ0})])],"isStart":false})]}),makeQuery(id+"F19.opExtrude","CAP_FACE",FACE,{"disambiguationData":[OSD([sQuery(id+"F17.wireOp",EDGE,"E47"),sQuery(id+"F17.wireOp",EDGE,"E48.2"),subQ4,subQ3,sQuery(id+"F17.wireOp",EDGE,"E57.2"),subQ2,subQ1,subQ0])],"isStart":false})],"blendedInto":[makeQuery(id+"F19.opExtrude","CAP_FACE",FACE,{"disambiguationData":[OSD([sQuery(id+"F17.wireOp",EDGE,"E47"),sQuery(id+"F17.wireOp",EDGE,"E48.2"),subQ4,subQ3,sQuery(id+"F17.wireOp",EDGE,"E57.2"),subQ2,subQ1,subQ0])],"isStart":false})]});}
            var Q7;
            {var subQ0=sQuery(id+"F17.wireOp",EDGE,"E63.2.0");Q7=makeQuery(id+"F22.opChamfer","BLEND_EDGE",EDGE,{"blendedFrom":[makeQuery(id+"F18.opExtrude","CAP_EDGE",EDGE,{"disambiguationData":[OSD([subQ0])],"isStart":false}),makeQuery(id+"F18.opExtrude","CAP_FACE",FACE,{"disambiguationData":[OSD([sQuery(id+"F17.wireOp",EDGE,"E46"),sQuery(id+"F17.wireOp",EDGE,"E49"),sQuery(id+"F17.wireOp",EDGE,"E50"),sQuery(id+"F17.wireOp",EDGE,"E51"),sQuery(id+"F17.wireOp",EDGE,"E52"),sQuery(id+"F17.wireOp",EDGE,"E53"),sQuery(id+"F17.wireOp",EDGE,"E54"),sQuery(id+"F17.wireOp",EDGE,"E55"),sQuery(id+"F17.wireOp",EDGE,"E56"),sQuery(id+"F17.wireOp",EDGE,"E62"),sQuery(id+"F17.wireOp",EDGE,"E63.1.0"),subQ0,sQuery(id+"F17.wireOp",EDGE,"E63.3.0")])],"isStart":false})],"blendedInto":[makeQuery(id+"F18.opExtrude","CAP_FACE",FACE,{"disambiguationData":[OSD([sQuery(id+"F17.wireOp",EDGE,"E46"),sQuery(id+"F17.wireOp",EDGE,"E49"),sQuery(id+"F17.wireOp",EDGE,"E50"),sQuery(id+"F17.wireOp",EDGE,"E51"),sQuery(id+"F17.wireOp",EDGE,"E52"),sQuery(id+"F17.wireOp",EDGE,"E53"),sQuery(id+"F17.wireOp",EDGE,"E54"),sQuery(id+"F17.wireOp",EDGE,"E55"),sQuery(id+"F17.wireOp",EDGE,"E56"),sQuery(id+"F17.wireOp",EDGE,"E62"),sQuery(id+"F17.wireOp",EDGE,"E63.1.0"),subQ0,sQuery(id+"F17.wireOp",EDGE,"E63.3.0")])],"isStart":false})]});}
            fillet(context, id + "F23", {"entities" : qUnion([Q0, Q1, Q2, Q3, Q4, Q5, Q6, Q7]), "radius" : 10 * mm, "tangentPropagation" : true, "allowEdgeOverflow" : false});
        }
    });
